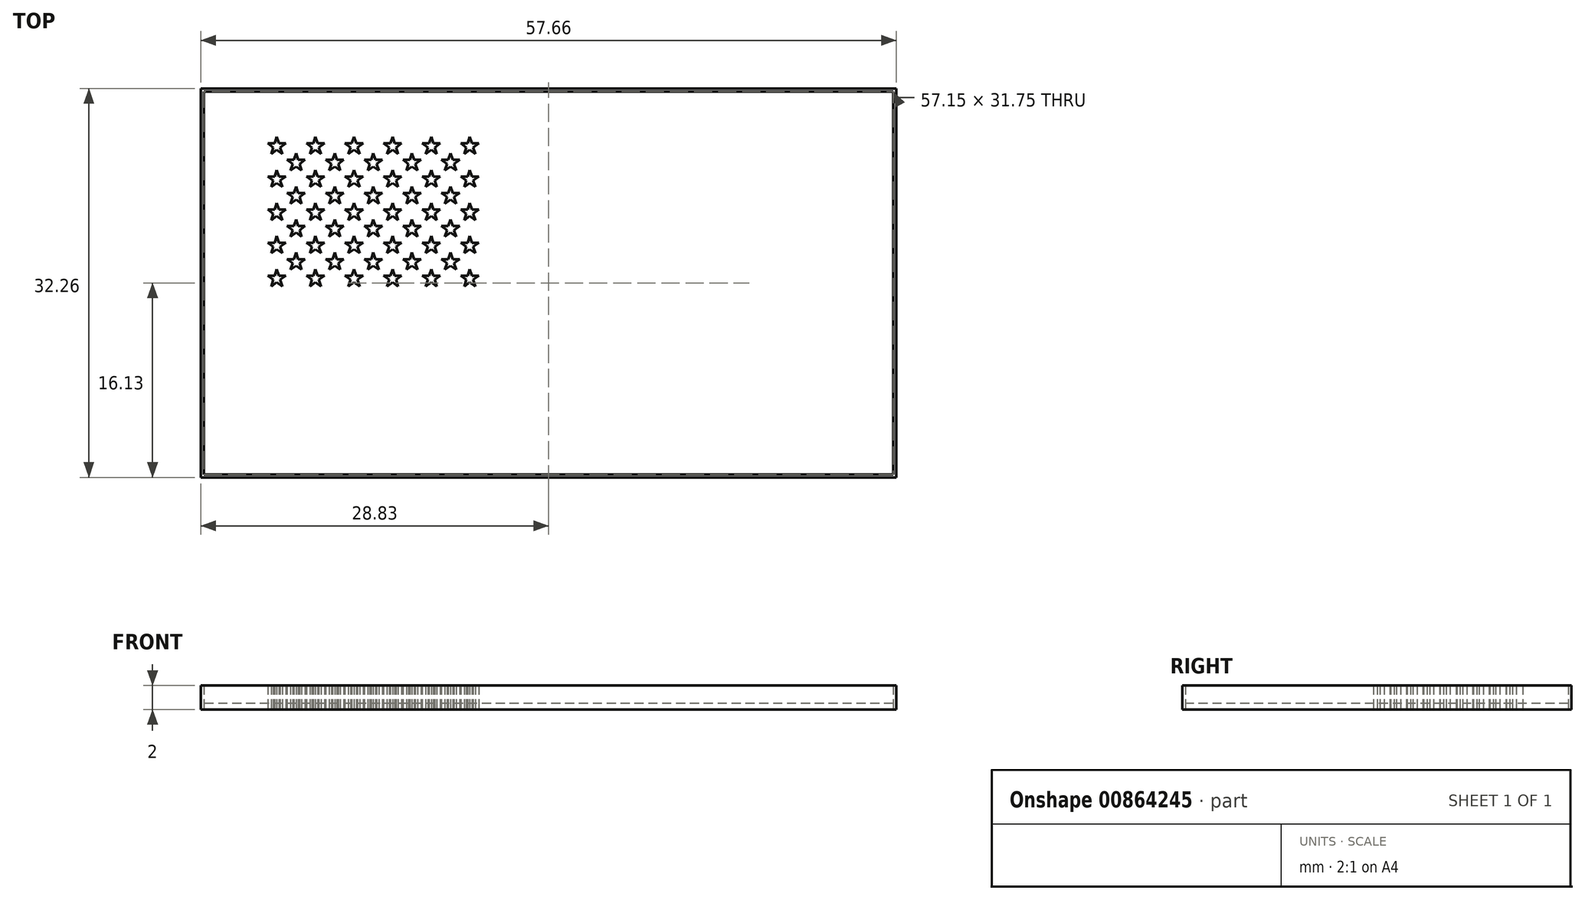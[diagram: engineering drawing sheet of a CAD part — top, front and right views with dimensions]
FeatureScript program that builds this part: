
annotation { "Feature Type Name" : "Feature", "Feature Type Description" : "" }
export const myFeature = defineFeature(function(context is Context, id is Id, definition is map)
    precondition{}
    {
        {
            var Q0;
            Q0=qCreatedBy(makeId("Top.planeOp"),FACE);
            var sketch = newSketch(context, id + "F0", { "sketchPlane" : qUnion([Q0])});
            skLineSegment(sketch, "E0.rect.bottom", {"start": v(24.13, 12.7) * mm, "end": v(-24.13, 12.7) * mm});
            skLineSegment(sketch, "E0.rect.top", {"start": v(24.13, -12.7) * mm, "end": v(-24.13, -12.7) * mm});
            skLineSegment(sketch, "E0.rect.left", {"start": v(24.13, 12.7) * mm, "end": v(24.13, -12.7) * mm});
            skLineSegment(sketch, "E0.rect.right", {"start": v(-24.13, 12.7) * mm, "end": v(-24.13, -12.7) * mm});
            skPoint(sketch, "E0.rect.middle", {"position": v(0, 0) * mm});
            skLineSegment(sketch, "E1.bottom", {"start": v(-24.13, 12.7) * mm, "end": v(-4.83, 12.7) * mm});
            skLineSegment(sketch, "E1.top", {"start": v(-24.13, -0.98) * mm, "end": v(-4.83, -0.98) * mm});
            skLineSegment(sketch, "E1.left", {"start": v(-24.13, 12.7) * mm, "end": v(-24.13, -0.98) * mm});
            skLineSegment(sketch, "E1.right", {"start": v(-4.83, 12.7) * mm, "end": v(-4.83, -0.98) * mm});
            skLineSegment(sketch, "E2.bottom", {"start": v(-4.83, 12.7) * mm, "end": v(24.13, 12.7) * mm});
            skLineSegment(sketch, "E2.top", {"start": v(-4.83, 10.75) * mm, "end": v(24.13, 10.75) * mm});
            skLineSegment(sketch, "E2.left", {"start": v(-4.83, 12.7) * mm, "end": v(-4.83, 10.75) * mm});
            skLineSegment(sketch, "E2.right", {"start": v(24.13, 12.7) * mm, "end": v(24.13, 10.75) * mm});
            skLineSegment(sketch, "E3.MirrorCS", {"start": v(-4.83, 8.8) * mm, "end": v(24.13, 8.8) * mm});
            skLineSegment(sketch, "E4.MirrorCS", {"start": v(-4.83, 6.84) * mm, "end": v(24.13, 6.84) * mm});
            skLineSegment(sketch, "E5.MirrorCS", {"start": v(-4.83, 4.89) * mm, "end": v(24.13, 4.89) * mm});
            skLineSegment(sketch, "E6.MirrorCS", {"start": v(-4.83, 2.93) * mm, "end": v(24.13, 2.93) * mm});
            skLineSegment(sketch, "E7.MirrorCS", {"start": v(-4.83, 0.98) * mm, "end": v(24.13, 0.98) * mm});
            skLineSegment(sketch, "E8.MirrorCS", {"start": v(-4.83, -0.97) * mm, "end": v(24.13, -0.97) * mm});
            skLineSegment(sketch, "E9.bottom", {"start": v(-24.13, -0.98) * mm, "end": v(24.13, -0.98) * mm});
            skLineSegment(sketch, "E9.top", {"start": v(-24.13, -2.93) * mm, "end": v(24.13, -2.93) * mm});
            skLineSegment(sketch, "E9.left", {"start": v(-24.13, -0.98) * mm, "end": v(-24.13, -2.93) * mm});
            skLineSegment(sketch, "E9.right", {"start": v(24.13, -0.98) * mm, "end": v(24.13, -2.93) * mm});
            skLineSegment(sketch, "E10.MirrorCS", {"start": v(-24.13, -4.88) * mm, "end": v(24.13, -4.88) * mm});
            skLineSegment(sketch, "E11.MirrorCS", {"start": v(-24.13, -6.84) * mm, "end": v(24.13, -6.84) * mm});
            skLineSegment(sketch, "E12.MirrorCS", {"start": v(-24.13, -8.8) * mm, "end": v(24.13, -8.8) * mm});
            skLineSegment(sketch, "E13.MirrorCS", {"start": v(-24.13, -10.74) * mm, "end": v(24.13, -10.74) * mm});
            skLineSegment(sketch, "E14.bottom", {"start": v(-24.13, 12.7) * mm, "end": v(-22.53, 12.7) * mm});
            skLineSegment(sketch, "E14.left", {"start": v(-24.13, 12.7) * mm, "end": v(-24.13, 11.33) * mm});
            skPoint(sketch, "E15.cCircle.perimeterSnap0", {"position": v(-22.53, 12.01) * mm});
            skPoint(sketch, "E15.0.startSnap0", {"position": v(-22.53, 12.01) * mm});
            skLineSegment(sketch, "E16", {"start": v(-22.53, 12.12) * mm, "end": v(-22.35, 11.57) * mm});
            skLineSegment(sketch, "E17", {"start": v(-21.78, 11.57) * mm, "end": v(-22.35, 11.57) * mm});
            skLineSegment(sketch, "E18", {"start": v(-23, 10.7) * mm, "end": v(-22.82, 11.24) * mm});
            skLineSegment(sketch, "E19", {"start": v(-23.28, 11.57) * mm, "end": v(-22.82, 11.24) * mm});
            skLineSegment(sketch, "E20", {"start": v(-21.78, 11.57) * mm, "end": v(-22.24, 11.24) * mm});
            skLineSegment(sketch, "E21.trimOffspring", {"start": v(-22.24, 11.24) * mm, "end": v(-22.07, 10.7) * mm});
            skLineSegment(sketch, "E22.trimOffspring", {"start": v(-22.53, 11.03) * mm, "end": v(-23, 10.7) * mm});
            skLineSegment(sketch, "E23.trimOffspring", {"start": v(-22.53, 11.03) * mm, "end": v(-22.07, 10.7) * mm});
            skLineSegment(sketch, "E24.trimOffspring", {"start": v(-22.7, 11.57) * mm, "end": v(-22.53, 12.12) * mm});
            skLineSegment(sketch, "E25.trimOffspring", {"start": v(-22.7, 11.57) * mm, "end": v(-23.28, 11.57) * mm});
            skLineSegment(sketch, "E26.0.1.0", {"start": v(-22.53, 9.37) * mm, "end": v(-22.35, 8.83) * mm});
            skLineSegment(sketch, "E26.0.1.1", {"start": v(-21.78, 8.83) * mm, "end": v(-22.35, 8.83) * mm});
            skLineSegment(sketch, "E26.0.1.2", {"start": v(-21.78, 8.83) * mm, "end": v(-22.24, 8.5) * mm});
            skLineSegment(sketch, "E26.0.1.3", {"start": v(-22.24, 8.5) * mm, "end": v(-22.07, 7.95) * mm});
            skLineSegment(sketch, "E26.0.1.4", {"start": v(-22.53, 8.28) * mm, "end": v(-22.07, 7.95) * mm});
            skLineSegment(sketch, "E26.0.1.5", {"start": v(-22.53, 8.28) * mm, "end": v(-23, 7.95) * mm});
            skLineSegment(sketch, "E26.0.1.6", {"start": v(-23, 7.95) * mm, "end": v(-22.82, 8.5) * mm});
            skLineSegment(sketch, "E26.0.1.7", {"start": v(-23.28, 8.83) * mm, "end": v(-22.82, 8.5) * mm});
            skLineSegment(sketch, "E26.0.1.8", {"start": v(-22.7, 8.83) * mm, "end": v(-22.53, 9.37) * mm});
            skLineSegment(sketch, "E26.0.1.9", {"start": v(-22.7, 8.83) * mm, "end": v(-23.28, 8.83) * mm});
            skLineSegment(sketch, "E26.0.2.0", {"start": v(-22.53, 6.63) * mm, "end": v(-22.35, 6.09) * mm});
            skLineSegment(sketch, "E26.0.2.1", {"start": v(-21.78, 6.09) * mm, "end": v(-22.35, 6.09) * mm});
            skLineSegment(sketch, "E26.0.2.2", {"start": v(-21.78, 6.09) * mm, "end": v(-22.24, 5.75) * mm});
            skLineSegment(sketch, "E26.0.2.3", {"start": v(-22.24, 5.75) * mm, "end": v(-22.07, 5.2) * mm});
            skLineSegment(sketch, "E26.0.2.4", {"start": v(-22.53, 5.54) * mm, "end": v(-22.07, 5.2) * mm});
            skLineSegment(sketch, "E26.0.2.5", {"start": v(-22.53, 5.54) * mm, "end": v(-23, 5.2) * mm});
            skLineSegment(sketch, "E26.0.2.6", {"start": v(-23, 5.2) * mm, "end": v(-22.82, 5.75) * mm});
            skLineSegment(sketch, "E26.0.2.7", {"start": v(-23.28, 6.09) * mm, "end": v(-22.82, 5.75) * mm});
            skLineSegment(sketch, "E26.0.2.8", {"start": v(-22.7, 6.09) * mm, "end": v(-22.53, 6.63) * mm});
            skLineSegment(sketch, "E26.0.2.9", {"start": v(-22.7, 6.09) * mm, "end": v(-23.28, 6.09) * mm});
            skLineSegment(sketch, "E26.0.3.0", {"start": v(-22.53, 3.89) * mm, "end": v(-22.35, 3.34) * mm});
            skLineSegment(sketch, "E26.0.3.1", {"start": v(-21.78, 3.34) * mm, "end": v(-22.35, 3.34) * mm});
            skLineSegment(sketch, "E26.0.3.2", {"start": v(-21.78, 3.34) * mm, "end": v(-22.24, 3) * mm});
            skLineSegment(sketch, "E26.0.3.3", {"start": v(-22.24, 3) * mm, "end": v(-22.07, 2.46) * mm});
            skLineSegment(sketch, "E26.0.3.4", {"start": v(-22.53, 2.8) * mm, "end": v(-22.07, 2.46) * mm});
            skLineSegment(sketch, "E26.0.3.5", {"start": v(-22.53, 2.8) * mm, "end": v(-23, 2.46) * mm});
            skLineSegment(sketch, "E26.0.3.6", {"start": v(-23, 2.46) * mm, "end": v(-22.82, 3) * mm});
            skLineSegment(sketch, "E26.0.3.7", {"start": v(-23.28, 3.34) * mm, "end": v(-22.82, 3) * mm});
            skLineSegment(sketch, "E26.0.3.8", {"start": v(-22.7, 3.34) * mm, "end": v(-22.53, 3.89) * mm});
            skLineSegment(sketch, "E26.0.3.9", {"start": v(-22.7, 3.34) * mm, "end": v(-23.28, 3.34) * mm});
            skLineSegment(sketch, "E26.0.4.0", {"start": v(-22.53, 1.14) * mm, "end": v(-22.35, 0.6) * mm});
            skLineSegment(sketch, "E26.0.4.1", {"start": v(-21.78, 0.6) * mm, "end": v(-22.35, 0.6) * mm});
            skLineSegment(sketch, "E26.0.4.2", {"start": v(-21.78, 0.6) * mm, "end": v(-22.24, 0.26) * mm});
            skLineSegment(sketch, "E26.0.4.3", {"start": v(-22.24, 0.26) * mm, "end": v(-22.07, -0.28) * mm});
            skLineSegment(sketch, "E26.0.4.4", {"start": v(-22.53, 0.05) * mm, "end": v(-22.07, -0.28) * mm});
            skLineSegment(sketch, "E26.0.4.5", {"start": v(-22.53, 0.05) * mm, "end": v(-23, -0.28) * mm});
            skLineSegment(sketch, "E26.0.4.6", {"start": v(-23, -0.28) * mm, "end": v(-22.82, 0.26) * mm});
            skLineSegment(sketch, "E26.0.4.7", {"start": v(-23.28, 0.6) * mm, "end": v(-22.82, 0.26) * mm});
            skLineSegment(sketch, "E26.0.4.8", {"start": v(-22.7, 0.6) * mm, "end": v(-22.53, 1.14) * mm});
            skLineSegment(sketch, "E26.0.4.9", {"start": v(-22.7, 0.6) * mm, "end": v(-23.28, 0.6) * mm});
            skLineSegment(sketch, "E26.1.0.0", {"start": v(-19.33, 12.12) * mm, "end": v(-19.15, 11.57) * mm});
            skLineSegment(sketch, "E26.1.0.1", {"start": v(-18.58, 11.57) * mm, "end": v(-19.15, 11.57) * mm});
            skLineSegment(sketch, "E26.1.0.2", {"start": v(-18.58, 11.57) * mm, "end": v(-19.04, 11.24) * mm});
            skLineSegment(sketch, "E26.1.0.3", {"start": v(-19.04, 11.24) * mm, "end": v(-18.87, 10.7) * mm});
            skLineSegment(sketch, "E26.1.0.4", {"start": v(-19.33, 11.03) * mm, "end": v(-18.87, 10.7) * mm});
            skLineSegment(sketch, "E26.1.0.5", {"start": v(-19.33, 11.03) * mm, "end": v(-19.8, 10.7) * mm});
            skLineSegment(sketch, "E26.1.0.6", {"start": v(-19.8, 10.7) * mm, "end": v(-19.62, 11.24) * mm});
            skLineSegment(sketch, "E26.1.0.7", {"start": v(-20.08, 11.57) * mm, "end": v(-19.62, 11.24) * mm});
            skLineSegment(sketch, "E26.1.0.8", {"start": v(-19.5, 11.57) * mm, "end": v(-19.33, 12.12) * mm});
            skLineSegment(sketch, "E26.1.0.9", {"start": v(-19.5, 11.57) * mm, "end": v(-20.08, 11.57) * mm});
            skLineSegment(sketch, "E26.1.1.0", {"start": v(-19.33, 9.37) * mm, "end": v(-19.15, 8.83) * mm});
            skLineSegment(sketch, "E26.1.1.1", {"start": v(-18.58, 8.83) * mm, "end": v(-19.15, 8.83) * mm});
            skLineSegment(sketch, "E26.1.1.2", {"start": v(-18.58, 8.83) * mm, "end": v(-19.04, 8.5) * mm});
            skLineSegment(sketch, "E26.1.1.3", {"start": v(-19.04, 8.5) * mm, "end": v(-18.87, 7.95) * mm});
            skLineSegment(sketch, "E26.1.1.4", {"start": v(-19.33, 8.28) * mm, "end": v(-18.87, 7.95) * mm});
            skLineSegment(sketch, "E26.1.1.5", {"start": v(-19.33, 8.28) * mm, "end": v(-19.8, 7.95) * mm});
            skLineSegment(sketch, "E26.1.1.6", {"start": v(-19.8, 7.95) * mm, "end": v(-19.62, 8.5) * mm});
            skLineSegment(sketch, "E26.1.1.7", {"start": v(-20.08, 8.83) * mm, "end": v(-19.62, 8.5) * mm});
            skLineSegment(sketch, "E26.1.1.8", {"start": v(-19.5, 8.83) * mm, "end": v(-19.33, 9.37) * mm});
            skLineSegment(sketch, "E26.1.1.9", {"start": v(-19.5, 8.83) * mm, "end": v(-20.08, 8.83) * mm});
            skLineSegment(sketch, "E26.1.2.0", {"start": v(-19.33, 6.63) * mm, "end": v(-19.15, 6.09) * mm});
            skLineSegment(sketch, "E26.1.2.1", {"start": v(-18.58, 6.09) * mm, "end": v(-19.15, 6.09) * mm});
            skLineSegment(sketch, "E26.1.2.2", {"start": v(-18.58, 6.09) * mm, "end": v(-19.04, 5.75) * mm});
            skLineSegment(sketch, "E26.1.2.3", {"start": v(-19.04, 5.75) * mm, "end": v(-18.87, 5.2) * mm});
            skLineSegment(sketch, "E26.1.2.4", {"start": v(-19.33, 5.54) * mm, "end": v(-18.87, 5.2) * mm});
            skLineSegment(sketch, "E26.1.2.5", {"start": v(-19.33, 5.54) * mm, "end": v(-19.8, 5.2) * mm});
            skLineSegment(sketch, "E26.1.2.6", {"start": v(-19.8, 5.2) * mm, "end": v(-19.62, 5.75) * mm});
            skLineSegment(sketch, "E26.1.2.7", {"start": v(-20.08, 6.09) * mm, "end": v(-19.62, 5.75) * mm});
            skLineSegment(sketch, "E26.1.2.8", {"start": v(-19.5, 6.09) * mm, "end": v(-19.33, 6.63) * mm});
            skLineSegment(sketch, "E26.1.2.9", {"start": v(-19.5, 6.09) * mm, "end": v(-20.08, 6.09) * mm});
            skLineSegment(sketch, "E26.1.3.0", {"start": v(-19.33, 3.89) * mm, "end": v(-19.15, 3.34) * mm});
            skLineSegment(sketch, "E26.1.3.1", {"start": v(-18.58, 3.34) * mm, "end": v(-19.15, 3.34) * mm});
            skLineSegment(sketch, "E26.1.3.2", {"start": v(-18.58, 3.34) * mm, "end": v(-19.04, 3) * mm});
            skLineSegment(sketch, "E26.1.3.3", {"start": v(-19.04, 3) * mm, "end": v(-18.87, 2.46) * mm});
            skLineSegment(sketch, "E26.1.3.4", {"start": v(-19.33, 2.8) * mm, "end": v(-18.87, 2.46) * mm});
            skLineSegment(sketch, "E26.1.3.5", {"start": v(-19.33, 2.8) * mm, "end": v(-19.8, 2.46) * mm});
            skLineSegment(sketch, "E26.1.3.6", {"start": v(-19.8, 2.46) * mm, "end": v(-19.62, 3) * mm});
            skLineSegment(sketch, "E26.1.3.7", {"start": v(-20.08, 3.34) * mm, "end": v(-19.62, 3) * mm});
            skLineSegment(sketch, "E26.1.3.8", {"start": v(-19.5, 3.34) * mm, "end": v(-19.33, 3.89) * mm});
            skLineSegment(sketch, "E26.1.3.9", {"start": v(-19.5, 3.34) * mm, "end": v(-20.08, 3.34) * mm});
            skLineSegment(sketch, "E26.1.4.0", {"start": v(-19.33, 1.14) * mm, "end": v(-19.15, 0.6) * mm});
            skLineSegment(sketch, "E26.1.4.1", {"start": v(-18.58, 0.6) * mm, "end": v(-19.15, 0.6) * mm});
            skLineSegment(sketch, "E26.1.4.2", {"start": v(-18.58, 0.6) * mm, "end": v(-19.04, 0.26) * mm});
            skLineSegment(sketch, "E26.1.4.3", {"start": v(-19.04, 0.26) * mm, "end": v(-18.87, -0.28) * mm});
            skLineSegment(sketch, "E26.1.4.4", {"start": v(-19.33, 0.05) * mm, "end": v(-18.87, -0.28) * mm});
            skLineSegment(sketch, "E26.1.4.5", {"start": v(-19.33, 0.05) * mm, "end": v(-19.8, -0.28) * mm});
            skLineSegment(sketch, "E26.1.4.6", {"start": v(-19.8, -0.28) * mm, "end": v(-19.62, 0.26) * mm});
            skLineSegment(sketch, "E26.1.4.7", {"start": v(-20.08, 0.6) * mm, "end": v(-19.62, 0.26) * mm});
            skLineSegment(sketch, "E26.1.4.8", {"start": v(-19.5, 0.6) * mm, "end": v(-19.33, 1.14) * mm});
            skLineSegment(sketch, "E26.1.4.9", {"start": v(-19.5, 0.6) * mm, "end": v(-20.08, 0.6) * mm});
            skLineSegment(sketch, "E26.2.0.0", {"start": v(-16.13, 12.12) * mm, "end": v(-15.95, 11.57) * mm});
            skLineSegment(sketch, "E26.2.0.1", {"start": v(-15.38, 11.57) * mm, "end": v(-15.95, 11.57) * mm});
            skLineSegment(sketch, "E26.2.0.2", {"start": v(-15.38, 11.57) * mm, "end": v(-15.84, 11.24) * mm});
            skLineSegment(sketch, "E26.2.0.3", {"start": v(-15.84, 11.24) * mm, "end": v(-15.67, 10.7) * mm});
            skLineSegment(sketch, "E26.2.0.4", {"start": v(-16.13, 11.03) * mm, "end": v(-15.67, 10.7) * mm});
            skLineSegment(sketch, "E26.2.0.5", {"start": v(-16.13, 11.03) * mm, "end": v(-16.6, 10.7) * mm});
            skLineSegment(sketch, "E26.2.0.6", {"start": v(-16.6, 10.7) * mm, "end": v(-16.42, 11.24) * mm});
            skLineSegment(sketch, "E26.2.0.7", {"start": v(-16.88, 11.57) * mm, "end": v(-16.42, 11.24) * mm});
            skLineSegment(sketch, "E26.2.0.8", {"start": v(-16.3, 11.57) * mm, "end": v(-16.13, 12.12) * mm});
            skLineSegment(sketch, "E26.2.0.9", {"start": v(-16.3, 11.57) * mm, "end": v(-16.88, 11.57) * mm});
            skLineSegment(sketch, "E26.2.1.0", {"start": v(-16.13, 9.37) * mm, "end": v(-15.95, 8.83) * mm});
            skLineSegment(sketch, "E26.2.1.1", {"start": v(-15.38, 8.83) * mm, "end": v(-15.95, 8.83) * mm});
            skLineSegment(sketch, "E26.2.1.2", {"start": v(-15.38, 8.83) * mm, "end": v(-15.84, 8.5) * mm});
            skLineSegment(sketch, "E26.2.1.3", {"start": v(-15.84, 8.5) * mm, "end": v(-15.67, 7.95) * mm});
            skLineSegment(sketch, "E26.2.1.4", {"start": v(-16.13, 8.28) * mm, "end": v(-15.67, 7.95) * mm});
            skLineSegment(sketch, "E26.2.1.5", {"start": v(-16.13, 8.28) * mm, "end": v(-16.6, 7.95) * mm});
            skLineSegment(sketch, "E26.2.1.6", {"start": v(-16.6, 7.95) * mm, "end": v(-16.42, 8.5) * mm});
            skLineSegment(sketch, "E26.2.1.7", {"start": v(-16.88, 8.83) * mm, "end": v(-16.42, 8.5) * mm});
            skLineSegment(sketch, "E26.2.1.8", {"start": v(-16.3, 8.83) * mm, "end": v(-16.13, 9.37) * mm});
            skLineSegment(sketch, "E26.2.1.9", {"start": v(-16.3, 8.83) * mm, "end": v(-16.88, 8.83) * mm});
            skLineSegment(sketch, "E26.2.2.0", {"start": v(-16.13, 6.63) * mm, "end": v(-15.95, 6.09) * mm});
            skLineSegment(sketch, "E26.2.2.1", {"start": v(-15.38, 6.09) * mm, "end": v(-15.95, 6.09) * mm});
            skLineSegment(sketch, "E26.2.2.2", {"start": v(-15.38, 6.09) * mm, "end": v(-15.84, 5.75) * mm});
            skLineSegment(sketch, "E26.2.2.3", {"start": v(-15.84, 5.75) * mm, "end": v(-15.67, 5.2) * mm});
            skLineSegment(sketch, "E26.2.2.4", {"start": v(-16.13, 5.54) * mm, "end": v(-15.67, 5.2) * mm});
            skLineSegment(sketch, "E26.2.2.5", {"start": v(-16.13, 5.54) * mm, "end": v(-16.6, 5.2) * mm});
            skLineSegment(sketch, "E26.2.2.6", {"start": v(-16.6, 5.2) * mm, "end": v(-16.42, 5.75) * mm});
            skLineSegment(sketch, "E26.2.2.7", {"start": v(-16.88, 6.09) * mm, "end": v(-16.42, 5.75) * mm});
            skLineSegment(sketch, "E26.2.2.8", {"start": v(-16.3, 6.09) * mm, "end": v(-16.13, 6.63) * mm});
            skLineSegment(sketch, "E26.2.2.9", {"start": v(-16.3, 6.09) * mm, "end": v(-16.88, 6.09) * mm});
            skLineSegment(sketch, "E26.2.3.0", {"start": v(-16.13, 3.89) * mm, "end": v(-15.95, 3.34) * mm});
            skLineSegment(sketch, "E26.2.3.1", {"start": v(-15.38, 3.34) * mm, "end": v(-15.95, 3.34) * mm});
            skLineSegment(sketch, "E26.2.3.2", {"start": v(-15.38, 3.34) * mm, "end": v(-15.84, 3) * mm});
            skLineSegment(sketch, "E26.2.3.3", {"start": v(-15.84, 3) * mm, "end": v(-15.67, 2.46) * mm});
            skLineSegment(sketch, "E26.2.3.4", {"start": v(-16.13, 2.8) * mm, "end": v(-15.67, 2.46) * mm});
            skLineSegment(sketch, "E26.2.3.5", {"start": v(-16.13, 2.8) * mm, "end": v(-16.6, 2.46) * mm});
            skLineSegment(sketch, "E26.2.3.6", {"start": v(-16.6, 2.46) * mm, "end": v(-16.42, 3) * mm});
            skLineSegment(sketch, "E26.2.3.7", {"start": v(-16.88, 3.34) * mm, "end": v(-16.42, 3) * mm});
            skLineSegment(sketch, "E26.2.3.8", {"start": v(-16.3, 3.34) * mm, "end": v(-16.13, 3.89) * mm});
            skLineSegment(sketch, "E26.2.3.9", {"start": v(-16.3, 3.34) * mm, "end": v(-16.88, 3.34) * mm});
            skLineSegment(sketch, "E26.2.4.0", {"start": v(-16.13, 1.14) * mm, "end": v(-15.95, 0.6) * mm});
            skLineSegment(sketch, "E26.2.4.1", {"start": v(-15.38, 0.6) * mm, "end": v(-15.95, 0.6) * mm});
            skLineSegment(sketch, "E26.2.4.2", {"start": v(-15.38, 0.6) * mm, "end": v(-15.84, 0.26) * mm});
            skLineSegment(sketch, "E26.2.4.3", {"start": v(-15.84, 0.26) * mm, "end": v(-15.67, -0.28) * mm});
            skLineSegment(sketch, "E26.2.4.4", {"start": v(-16.13, 0.05) * mm, "end": v(-15.67, -0.28) * mm});
            skLineSegment(sketch, "E26.2.4.5", {"start": v(-16.13, 0.05) * mm, "end": v(-16.6, -0.28) * mm});
            skLineSegment(sketch, "E26.2.4.6", {"start": v(-16.6, -0.28) * mm, "end": v(-16.42, 0.26) * mm});
            skLineSegment(sketch, "E26.2.4.7", {"start": v(-16.88, 0.6) * mm, "end": v(-16.42, 0.26) * mm});
            skLineSegment(sketch, "E26.2.4.8", {"start": v(-16.3, 0.6) * mm, "end": v(-16.13, 1.14) * mm});
            skLineSegment(sketch, "E26.2.4.9", {"start": v(-16.3, 0.6) * mm, "end": v(-16.88, 0.6) * mm});
            skLineSegment(sketch, "E26.3.0.0", {"start": v(-12.93, 12.12) * mm, "end": v(-12.75, 11.57) * mm});
            skLineSegment(sketch, "E26.3.0.1", {"start": v(-12.18, 11.57) * mm, "end": v(-12.75, 11.57) * mm});
            skLineSegment(sketch, "E26.3.0.2", {"start": v(-12.18, 11.57) * mm, "end": v(-12.64, 11.24) * mm});
            skLineSegment(sketch, "E26.3.0.3", {"start": v(-12.64, 11.24) * mm, "end": v(-12.47, 10.7) * mm});
            skLineSegment(sketch, "E26.3.0.4", {"start": v(-12.93, 11.03) * mm, "end": v(-12.47, 10.7) * mm});
            skLineSegment(sketch, "E26.3.0.5", {"start": v(-12.93, 11.03) * mm, "end": v(-13.4, 10.7) * mm});
            skLineSegment(sketch, "E26.3.0.6", {"start": v(-13.4, 10.7) * mm, "end": v(-13.21, 11.24) * mm});
            skLineSegment(sketch, "E26.3.0.7", {"start": v(-13.68, 11.57) * mm, "end": v(-13.21, 11.24) * mm});
            skLineSegment(sketch, "E26.3.0.8", {"start": v(-13.1, 11.57) * mm, "end": v(-12.93, 12.12) * mm});
            skLineSegment(sketch, "E26.3.0.9", {"start": v(-13.1, 11.57) * mm, "end": v(-13.68, 11.57) * mm});
            skLineSegment(sketch, "E26.3.1.0", {"start": v(-12.93, 9.37) * mm, "end": v(-12.75, 8.83) * mm});
            skLineSegment(sketch, "E26.3.1.1", {"start": v(-12.18, 8.83) * mm, "end": v(-12.75, 8.83) * mm});
            skLineSegment(sketch, "E26.3.1.2", {"start": v(-12.18, 8.83) * mm, "end": v(-12.64, 8.5) * mm});
            skLineSegment(sketch, "E26.3.1.3", {"start": v(-12.64, 8.5) * mm, "end": v(-12.47, 7.95) * mm});
            skLineSegment(sketch, "E26.3.1.4", {"start": v(-12.93, 8.28) * mm, "end": v(-12.47, 7.95) * mm});
            skLineSegment(sketch, "E26.3.1.5", {"start": v(-12.93, 8.28) * mm, "end": v(-13.4, 7.95) * mm});
            skLineSegment(sketch, "E26.3.1.6", {"start": v(-13.4, 7.95) * mm, "end": v(-13.21, 8.5) * mm});
            skLineSegment(sketch, "E26.3.1.7", {"start": v(-13.68, 8.83) * mm, "end": v(-13.21, 8.5) * mm});
            skLineSegment(sketch, "E26.3.1.8", {"start": v(-13.1, 8.83) * mm, "end": v(-12.93, 9.37) * mm});
            skLineSegment(sketch, "E26.3.1.9", {"start": v(-13.1, 8.83) * mm, "end": v(-13.68, 8.83) * mm});
            skLineSegment(sketch, "E26.3.2.0", {"start": v(-12.93, 6.63) * mm, "end": v(-12.75, 6.09) * mm});
            skLineSegment(sketch, "E26.3.2.1", {"start": v(-12.18, 6.09) * mm, "end": v(-12.75, 6.09) * mm});
            skLineSegment(sketch, "E26.3.2.2", {"start": v(-12.18, 6.09) * mm, "end": v(-12.64, 5.75) * mm});
            skLineSegment(sketch, "E26.3.2.3", {"start": v(-12.64, 5.75) * mm, "end": v(-12.47, 5.2) * mm});
            skLineSegment(sketch, "E26.3.2.4", {"start": v(-12.93, 5.54) * mm, "end": v(-12.47, 5.2) * mm});
            skLineSegment(sketch, "E26.3.2.5", {"start": v(-12.93, 5.54) * mm, "end": v(-13.4, 5.2) * mm});
            skLineSegment(sketch, "E26.3.2.6", {"start": v(-13.4, 5.2) * mm, "end": v(-13.21, 5.75) * mm});
            skLineSegment(sketch, "E26.3.2.7", {"start": v(-13.68, 6.09) * mm, "end": v(-13.21, 5.75) * mm});
            skLineSegment(sketch, "E26.3.2.8", {"start": v(-13.1, 6.09) * mm, "end": v(-12.93, 6.63) * mm});
            skLineSegment(sketch, "E26.3.2.9", {"start": v(-13.1, 6.09) * mm, "end": v(-13.68, 6.09) * mm});
            skLineSegment(sketch, "E26.3.3.0", {"start": v(-12.93, 3.89) * mm, "end": v(-12.75, 3.34) * mm});
            skLineSegment(sketch, "E26.3.3.1", {"start": v(-12.18, 3.34) * mm, "end": v(-12.75, 3.34) * mm});
            skLineSegment(sketch, "E26.3.3.2", {"start": v(-12.18, 3.34) * mm, "end": v(-12.64, 3) * mm});
            skLineSegment(sketch, "E26.3.3.3", {"start": v(-12.64, 3) * mm, "end": v(-12.47, 2.46) * mm});
            skLineSegment(sketch, "E26.3.3.4", {"start": v(-12.93, 2.8) * mm, "end": v(-12.47, 2.46) * mm});
            skLineSegment(sketch, "E26.3.3.5", {"start": v(-12.93, 2.8) * mm, "end": v(-13.4, 2.46) * mm});
            skLineSegment(sketch, "E26.3.3.6", {"start": v(-13.4, 2.46) * mm, "end": v(-13.21, 3) * mm});
            skLineSegment(sketch, "E26.3.3.7", {"start": v(-13.68, 3.34) * mm, "end": v(-13.21, 3) * mm});
            skLineSegment(sketch, "E26.3.3.8", {"start": v(-13.1, 3.34) * mm, "end": v(-12.93, 3.89) * mm});
            skLineSegment(sketch, "E26.3.3.9", {"start": v(-13.1, 3.34) * mm, "end": v(-13.68, 3.34) * mm});
            skLineSegment(sketch, "E26.3.4.0", {"start": v(-12.93, 1.14) * mm, "end": v(-12.75, 0.6) * mm});
            skLineSegment(sketch, "E26.3.4.1", {"start": v(-12.18, 0.6) * mm, "end": v(-12.75, 0.6) * mm});
            skLineSegment(sketch, "E26.3.4.2", {"start": v(-12.18, 0.6) * mm, "end": v(-12.64, 0.26) * mm});
            skLineSegment(sketch, "E26.3.4.3", {"start": v(-12.64, 0.26) * mm, "end": v(-12.47, -0.28) * mm});
            skLineSegment(sketch, "E26.3.4.4", {"start": v(-12.93, 0.05) * mm, "end": v(-12.47, -0.28) * mm});
            skLineSegment(sketch, "E26.3.4.5", {"start": v(-12.93, 0.05) * mm, "end": v(-13.4, -0.28) * mm});
            skLineSegment(sketch, "E26.3.4.6", {"start": v(-13.4, -0.28) * mm, "end": v(-13.21, 0.26) * mm});
            skLineSegment(sketch, "E26.3.4.7", {"start": v(-13.68, 0.6) * mm, "end": v(-13.21, 0.26) * mm});
            skLineSegment(sketch, "E26.3.4.8", {"start": v(-13.1, 0.6) * mm, "end": v(-12.93, 1.14) * mm});
            skLineSegment(sketch, "E26.3.4.9", {"start": v(-13.1, 0.6) * mm, "end": v(-13.68, 0.6) * mm});
            skLineSegment(sketch, "E26.4.0.0", {"start": v(-9.73, 12.12) * mm, "end": v(-9.55, 11.57) * mm});
            skLineSegment(sketch, "E26.4.0.1", {"start": v(-8.98, 11.57) * mm, "end": v(-9.55, 11.57) * mm});
            skLineSegment(sketch, "E26.4.0.2", {"start": v(-8.98, 11.57) * mm, "end": v(-9.44, 11.24) * mm});
            skLineSegment(sketch, "E26.4.0.3", {"start": v(-9.44, 11.24) * mm, "end": v(-9.27, 10.7) * mm});
            skLineSegment(sketch, "E26.4.0.4", {"start": v(-9.73, 11.03) * mm, "end": v(-9.27, 10.7) * mm});
            skLineSegment(sketch, "E26.4.0.5", {"start": v(-9.73, 11.03) * mm, "end": v(-10.2, 10.7) * mm});
            skLineSegment(sketch, "E26.4.0.6", {"start": v(-10.2, 10.7) * mm, "end": v(-10.01, 11.24) * mm});
            skLineSegment(sketch, "E26.4.0.7", {"start": v(-10.48, 11.57) * mm, "end": v(-10.01, 11.24) * mm});
            skLineSegment(sketch, "E26.4.0.8", {"start": v(-9.9, 11.57) * mm, "end": v(-9.73, 12.12) * mm});
            skLineSegment(sketch, "E26.4.0.9", {"start": v(-9.9, 11.57) * mm, "end": v(-10.48, 11.57) * mm});
            skLineSegment(sketch, "E26.4.1.0", {"start": v(-9.73, 9.37) * mm, "end": v(-9.55, 8.83) * mm});
            skLineSegment(sketch, "E26.4.1.1", {"start": v(-8.98, 8.83) * mm, "end": v(-9.55, 8.83) * mm});
            skLineSegment(sketch, "E26.4.1.2", {"start": v(-8.98, 8.83) * mm, "end": v(-9.44, 8.5) * mm});
            skLineSegment(sketch, "E26.4.1.3", {"start": v(-9.44, 8.5) * mm, "end": v(-9.27, 7.95) * mm});
            skLineSegment(sketch, "E26.4.1.4", {"start": v(-9.73, 8.28) * mm, "end": v(-9.27, 7.95) * mm});
            skLineSegment(sketch, "E26.4.1.5", {"start": v(-9.73, 8.28) * mm, "end": v(-10.2, 7.95) * mm});
            skLineSegment(sketch, "E26.4.1.6", {"start": v(-10.2, 7.95) * mm, "end": v(-10.01, 8.5) * mm});
            skLineSegment(sketch, "E26.4.1.7", {"start": v(-10.48, 8.83) * mm, "end": v(-10.01, 8.5) * mm});
            skLineSegment(sketch, "E26.4.1.8", {"start": v(-9.9, 8.83) * mm, "end": v(-9.73, 9.37) * mm});
            skLineSegment(sketch, "E26.4.1.9", {"start": v(-9.9, 8.83) * mm, "end": v(-10.48, 8.83) * mm});
            skLineSegment(sketch, "E26.4.2.0", {"start": v(-9.73, 6.63) * mm, "end": v(-9.55, 6.09) * mm});
            skLineSegment(sketch, "E26.4.2.1", {"start": v(-8.98, 6.09) * mm, "end": v(-9.55, 6.09) * mm});
            skLineSegment(sketch, "E26.4.2.2", {"start": v(-8.98, 6.09) * mm, "end": v(-9.44, 5.75) * mm});
            skLineSegment(sketch, "E26.4.2.3", {"start": v(-9.44, 5.75) * mm, "end": v(-9.27, 5.2) * mm});
            skLineSegment(sketch, "E26.4.2.4", {"start": v(-9.73, 5.54) * mm, "end": v(-9.27, 5.2) * mm});
            skLineSegment(sketch, "E26.4.2.5", {"start": v(-9.73, 5.54) * mm, "end": v(-10.2, 5.2) * mm});
            skLineSegment(sketch, "E26.4.2.6", {"start": v(-10.2, 5.2) * mm, "end": v(-10.01, 5.75) * mm});
            skLineSegment(sketch, "E26.4.2.7", {"start": v(-10.48, 6.09) * mm, "end": v(-10.01, 5.75) * mm});
            skLineSegment(sketch, "E26.4.2.8", {"start": v(-9.9, 6.09) * mm, "end": v(-9.73, 6.63) * mm});
            skLineSegment(sketch, "E26.4.2.9", {"start": v(-9.9, 6.09) * mm, "end": v(-10.48, 6.09) * mm});
            skLineSegment(sketch, "E26.4.3.0", {"start": v(-9.73, 3.89) * mm, "end": v(-9.55, 3.34) * mm});
            skLineSegment(sketch, "E26.4.3.1", {"start": v(-8.98, 3.34) * mm, "end": v(-9.55, 3.34) * mm});
            skLineSegment(sketch, "E26.4.3.2", {"start": v(-8.98, 3.34) * mm, "end": v(-9.44, 3) * mm});
            skLineSegment(sketch, "E26.4.3.3", {"start": v(-9.44, 3) * mm, "end": v(-9.27, 2.46) * mm});
            skLineSegment(sketch, "E26.4.3.4", {"start": v(-9.73, 2.8) * mm, "end": v(-9.27, 2.46) * mm});
            skLineSegment(sketch, "E26.4.3.5", {"start": v(-9.73, 2.8) * mm, "end": v(-10.2, 2.46) * mm});
            skLineSegment(sketch, "E26.4.3.6", {"start": v(-10.2, 2.46) * mm, "end": v(-10.01, 3) * mm});
            skLineSegment(sketch, "E26.4.3.7", {"start": v(-10.48, 3.34) * mm, "end": v(-10.01, 3) * mm});
            skLineSegment(sketch, "E26.4.3.8", {"start": v(-9.9, 3.34) * mm, "end": v(-9.73, 3.89) * mm});
            skLineSegment(sketch, "E26.4.3.9", {"start": v(-9.9, 3.34) * mm, "end": v(-10.48, 3.34) * mm});
            skLineSegment(sketch, "E26.4.4.0", {"start": v(-9.73, 1.14) * mm, "end": v(-9.55, 0.6) * mm});
            skLineSegment(sketch, "E26.4.4.1", {"start": v(-8.98, 0.6) * mm, "end": v(-9.55, 0.6) * mm});
            skLineSegment(sketch, "E26.4.4.2", {"start": v(-8.98, 0.6) * mm, "end": v(-9.44, 0.26) * mm});
            skLineSegment(sketch, "E26.4.4.3", {"start": v(-9.44, 0.26) * mm, "end": v(-9.27, -0.28) * mm});
            skLineSegment(sketch, "E26.4.4.4", {"start": v(-9.73, 0.05) * mm, "end": v(-9.27, -0.28) * mm});
            skLineSegment(sketch, "E26.4.4.5", {"start": v(-9.73, 0.05) * mm, "end": v(-10.2, -0.28) * mm});
            skLineSegment(sketch, "E26.4.4.6", {"start": v(-10.2, -0.28) * mm, "end": v(-10.01, 0.26) * mm});
            skLineSegment(sketch, "E26.4.4.7", {"start": v(-10.48, 0.6) * mm, "end": v(-10.01, 0.26) * mm});
            skLineSegment(sketch, "E26.4.4.8", {"start": v(-9.9, 0.6) * mm, "end": v(-9.73, 1.14) * mm});
            skLineSegment(sketch, "E26.4.4.9", {"start": v(-9.9, 0.6) * mm, "end": v(-10.48, 0.6) * mm});
            skLineSegment(sketch, "E26.5.0.0", {"start": v(-6.53, 12.12) * mm, "end": v(-6.35, 11.57) * mm});
            skLineSegment(sketch, "E26.5.0.1", {"start": v(-5.78, 11.57) * mm, "end": v(-6.35, 11.57) * mm});
            skLineSegment(sketch, "E26.5.0.2", {"start": v(-5.78, 11.57) * mm, "end": v(-6.24, 11.24) * mm});
            skLineSegment(sketch, "E26.5.0.3", {"start": v(-6.24, 11.24) * mm, "end": v(-6.06, 10.7) * mm});
            skLineSegment(sketch, "E26.5.0.4", {"start": v(-6.53, 11.03) * mm, "end": v(-6.06, 10.7) * mm});
            skLineSegment(sketch, "E26.5.0.5", {"start": v(-6.53, 11.03) * mm, "end": v(-7, 10.7) * mm});
            skLineSegment(sketch, "E26.5.0.6", {"start": v(-7, 10.7) * mm, "end": v(-6.81, 11.24) * mm});
            skLineSegment(sketch, "E26.5.0.7", {"start": v(-7.28, 11.57) * mm, "end": v(-6.81, 11.24) * mm});
            skLineSegment(sketch, "E26.5.0.8", {"start": v(-6.7, 11.57) * mm, "end": v(-6.53, 12.12) * mm});
            skLineSegment(sketch, "E26.5.0.9", {"start": v(-6.7, 11.57) * mm, "end": v(-7.28, 11.57) * mm});
            skLineSegment(sketch, "E26.5.1.0", {"start": v(-6.53, 9.37) * mm, "end": v(-6.35, 8.83) * mm});
            skLineSegment(sketch, "E26.5.1.1", {"start": v(-5.78, 8.83) * mm, "end": v(-6.35, 8.83) * mm});
            skLineSegment(sketch, "E26.5.1.2", {"start": v(-5.78, 8.83) * mm, "end": v(-6.24, 8.5) * mm});
            skLineSegment(sketch, "E26.5.1.3", {"start": v(-6.24, 8.5) * mm, "end": v(-6.06, 7.95) * mm});
            skLineSegment(sketch, "E26.5.1.4", {"start": v(-6.53, 8.28) * mm, "end": v(-6.06, 7.95) * mm});
            skLineSegment(sketch, "E26.5.1.5", {"start": v(-6.53, 8.28) * mm, "end": v(-7, 7.95) * mm});
            skLineSegment(sketch, "E26.5.1.6", {"start": v(-7, 7.95) * mm, "end": v(-6.81, 8.5) * mm});
            skLineSegment(sketch, "E26.5.1.7", {"start": v(-7.28, 8.83) * mm, "end": v(-6.81, 8.5) * mm});
            skLineSegment(sketch, "E26.5.1.8", {"start": v(-6.7, 8.83) * mm, "end": v(-6.53, 9.37) * mm});
            skLineSegment(sketch, "E26.5.1.9", {"start": v(-6.7, 8.83) * mm, "end": v(-7.28, 8.83) * mm});
            skLineSegment(sketch, "E26.5.2.0", {"start": v(-6.53, 6.63) * mm, "end": v(-6.35, 6.09) * mm});
            skLineSegment(sketch, "E26.5.2.1", {"start": v(-5.78, 6.09) * mm, "end": v(-6.35, 6.09) * mm});
            skLineSegment(sketch, "E26.5.2.2", {"start": v(-5.78, 6.09) * mm, "end": v(-6.24, 5.75) * mm});
            skLineSegment(sketch, "E26.5.2.3", {"start": v(-6.24, 5.75) * mm, "end": v(-6.06, 5.2) * mm});
            skLineSegment(sketch, "E26.5.2.4", {"start": v(-6.53, 5.54) * mm, "end": v(-6.06, 5.2) * mm});
            skLineSegment(sketch, "E26.5.2.5", {"start": v(-6.53, 5.54) * mm, "end": v(-7, 5.2) * mm});
            skLineSegment(sketch, "E26.5.2.6", {"start": v(-7, 5.2) * mm, "end": v(-6.81, 5.75) * mm});
            skLineSegment(sketch, "E26.5.2.7", {"start": v(-7.28, 6.09) * mm, "end": v(-6.81, 5.75) * mm});
            skLineSegment(sketch, "E26.5.2.8", {"start": v(-6.7, 6.09) * mm, "end": v(-6.53, 6.63) * mm});
            skLineSegment(sketch, "E26.5.2.9", {"start": v(-6.7, 6.09) * mm, "end": v(-7.28, 6.09) * mm});
            skLineSegment(sketch, "E26.5.3.0", {"start": v(-6.53, 3.89) * mm, "end": v(-6.35, 3.34) * mm});
            skLineSegment(sketch, "E26.5.3.1", {"start": v(-5.78, 3.34) * mm, "end": v(-6.35, 3.34) * mm});
            skLineSegment(sketch, "E26.5.3.2", {"start": v(-5.78, 3.34) * mm, "end": v(-6.24, 3) * mm});
            skLineSegment(sketch, "E26.5.3.3", {"start": v(-6.24, 3) * mm, "end": v(-6.06, 2.46) * mm});
            skLineSegment(sketch, "E26.5.3.4", {"start": v(-6.53, 2.8) * mm, "end": v(-6.06, 2.46) * mm});
            skLineSegment(sketch, "E26.5.3.5", {"start": v(-6.53, 2.8) * mm, "end": v(-7, 2.46) * mm});
            skLineSegment(sketch, "E26.5.3.6", {"start": v(-7, 2.46) * mm, "end": v(-6.81, 3) * mm});
            skLineSegment(sketch, "E26.5.3.7", {"start": v(-7.28, 3.34) * mm, "end": v(-6.81, 3) * mm});
            skLineSegment(sketch, "E26.5.3.8", {"start": v(-6.7, 3.34) * mm, "end": v(-6.53, 3.89) * mm});
            skLineSegment(sketch, "E26.5.3.9", {"start": v(-6.7, 3.34) * mm, "end": v(-7.28, 3.34) * mm});
            skLineSegment(sketch, "E26.5.4.0", {"start": v(-6.53, 1.14) * mm, "end": v(-6.35, 0.6) * mm});
            skLineSegment(sketch, "E26.5.4.1", {"start": v(-5.78, 0.6) * mm, "end": v(-6.35, 0.6) * mm});
            skLineSegment(sketch, "E26.5.4.2", {"start": v(-5.78, 0.6) * mm, "end": v(-6.24, 0.26) * mm});
            skLineSegment(sketch, "E26.5.4.3", {"start": v(-6.24, 0.26) * mm, "end": v(-6.06, -0.28) * mm});
            skLineSegment(sketch, "E26.5.4.4", {"start": v(-6.53, 0.05) * mm, "end": v(-6.06, -0.28) * mm});
            skLineSegment(sketch, "E26.5.4.5", {"start": v(-6.53, 0.05) * mm, "end": v(-7, -0.28) * mm});
            skLineSegment(sketch, "E26.5.4.6", {"start": v(-7, -0.28) * mm, "end": v(-6.81, 0.26) * mm});
            skLineSegment(sketch, "E26.5.4.7", {"start": v(-7.28, 0.6) * mm, "end": v(-6.81, 0.26) * mm});
            skLineSegment(sketch, "E26.5.4.8", {"start": v(-6.7, 0.6) * mm, "end": v(-6.53, 1.14) * mm});
            skLineSegment(sketch, "E26.5.4.9", {"start": v(-6.7, 0.6) * mm, "end": v(-7.28, 0.6) * mm});
            skLineSegment(sketch, "E26.direction1", {"start": v(-22.35, 11.57) * mm, "end": v(-19.15, 11.57) * mm, "construction": true});
            skLineSegment(sketch, "E26.direction2", {"start": v(-22.35, 11.57) * mm, "end": v(-22.35, 8.83) * mm, "construction": true});
            skPoint(sketch, "E27.cCircle.perimeterSnap0", {"position": v(-20.93, 10.64) * mm});
            skPoint(sketch, "E27.0.startSnap0", {"position": v(-20.93, 10.64) * mm});
            skLineSegment(sketch, "E28", {"start": v(-20.93, 10.75) * mm, "end": v(-20.75, 10.2) * mm});
            skLineSegment(sketch, "E29", {"start": v(-21.68, 10.2) * mm, "end": v(-21.1, 10.2) * mm});
            skLineSegment(sketch, "E30", {"start": v(-21.4, 9.32) * mm, "end": v(-20.93, 9.66) * mm});
            skLineSegment(sketch, "E31", {"start": v(-21.4, 9.32) * mm, "end": v(-21.22, 9.86) * mm});
            skLineSegment(sketch, "E32", {"start": v(-20.47, 9.32) * mm, "end": v(-20.93, 9.66) * mm});
            skLineSegment(sketch, "E33.trimOffspring", {"start": v(-20.64, 9.86) * mm, "end": v(-20.47, 9.32) * mm});
            skLineSegment(sketch, "E34.trimOffspring", {"start": v(-20.75, 10.2) * mm, "end": v(-20.18, 10.2) * mm});
            skLineSegment(sketch, "E35.trimOffspring", {"start": v(-21.1, 10.2) * mm, "end": v(-20.93, 10.75) * mm});
            skLineSegment(sketch, "E36.trimOffspring", {"start": v(-21.22, 9.86) * mm, "end": v(-21.68, 10.2) * mm});
            skLineSegment(sketch, "E37.trimOffspring", {"start": v(-20.64, 9.86) * mm, "end": v(-20.18, 10.2) * mm});
            skLineSegment(sketch, "E38.0.1.0", {"start": v(-20.93, 8) * mm, "end": v(-20.75, 7.46) * mm});
            skLineSegment(sketch, "E38.0.1.1", {"start": v(-20.75, 7.46) * mm, "end": v(-20.18, 7.46) * mm});
            skLineSegment(sketch, "E38.0.1.2", {"start": v(-20.64, 7.12) * mm, "end": v(-20.18, 7.46) * mm});
            skLineSegment(sketch, "E38.0.1.3", {"start": v(-20.64, 7.12) * mm, "end": v(-20.47, 6.57) * mm});
            skLineSegment(sketch, "E38.0.1.4", {"start": v(-20.47, 6.57) * mm, "end": v(-20.93, 6.91) * mm});
            skLineSegment(sketch, "E38.0.1.5", {"start": v(-21.4, 6.57) * mm, "end": v(-20.93, 6.91) * mm});
            skLineSegment(sketch, "E38.0.1.6", {"start": v(-21.4, 6.57) * mm, "end": v(-21.22, 7.12) * mm});
            skLineSegment(sketch, "E38.0.1.7", {"start": v(-21.22, 7.12) * mm, "end": v(-21.68, 7.46) * mm});
            skLineSegment(sketch, "E38.0.1.8", {"start": v(-21.68, 7.46) * mm, "end": v(-21.1, 7.46) * mm});
            skLineSegment(sketch, "E38.0.1.9", {"start": v(-21.1, 7.46) * mm, "end": v(-20.93, 8) * mm});
            skLineSegment(sketch, "E38.0.2.0", {"start": v(-20.93, 5.26) * mm, "end": v(-20.75, 4.71) * mm});
            skLineSegment(sketch, "E38.0.2.1", {"start": v(-20.75, 4.71) * mm, "end": v(-20.18, 4.71) * mm});
            skLineSegment(sketch, "E38.0.2.2", {"start": v(-20.64, 4.38) * mm, "end": v(-20.18, 4.71) * mm});
            skLineSegment(sketch, "E38.0.2.3", {"start": v(-20.64, 4.38) * mm, "end": v(-20.47, 3.83) * mm});
            skLineSegment(sketch, "E38.0.2.4", {"start": v(-20.47, 3.83) * mm, "end": v(-20.93, 4.17) * mm});
            skLineSegment(sketch, "E38.0.2.5", {"start": v(-21.4, 3.83) * mm, "end": v(-20.93, 4.17) * mm});
            skLineSegment(sketch, "E38.0.2.6", {"start": v(-21.4, 3.83) * mm, "end": v(-21.22, 4.38) * mm});
            skLineSegment(sketch, "E38.0.2.7", {"start": v(-21.22, 4.38) * mm, "end": v(-21.68, 4.71) * mm});
            skLineSegment(sketch, "E38.0.2.8", {"start": v(-21.68, 4.71) * mm, "end": v(-21.1, 4.71) * mm});
            skLineSegment(sketch, "E38.0.2.9", {"start": v(-21.1, 4.71) * mm, "end": v(-20.93, 5.26) * mm});
            skLineSegment(sketch, "E38.0.3.0", {"start": v(-20.93, 2.52) * mm, "end": v(-20.75, 1.97) * mm});
            skLineSegment(sketch, "E38.0.3.1", {"start": v(-20.75, 1.97) * mm, "end": v(-20.18, 1.97) * mm});
            skLineSegment(sketch, "E38.0.3.2", {"start": v(-20.64, 1.63) * mm, "end": v(-20.18, 1.97) * mm});
            skLineSegment(sketch, "E38.0.3.3", {"start": v(-20.64, 1.63) * mm, "end": v(-20.47, 1.09) * mm});
            skLineSegment(sketch, "E38.0.3.4", {"start": v(-20.47, 1.09) * mm, "end": v(-20.93, 1.43) * mm});
            skLineSegment(sketch, "E38.0.3.5", {"start": v(-21.4, 1.09) * mm, "end": v(-20.93, 1.43) * mm});
            skLineSegment(sketch, "E38.0.3.6", {"start": v(-21.4, 1.09) * mm, "end": v(-21.22, 1.63) * mm});
            skLineSegment(sketch, "E38.0.3.7", {"start": v(-21.22, 1.63) * mm, "end": v(-21.68, 1.97) * mm});
            skLineSegment(sketch, "E38.0.3.8", {"start": v(-21.68, 1.97) * mm, "end": v(-21.1, 1.97) * mm});
            skLineSegment(sketch, "E38.0.3.9", {"start": v(-21.1, 1.97) * mm, "end": v(-20.93, 2.52) * mm});
            skLineSegment(sketch, "E38.1.0.0", {"start": v(-17.73, 10.75) * mm, "end": v(-17.55, 10.2) * mm});
            skLineSegment(sketch, "E38.1.0.1", {"start": v(-17.55, 10.2) * mm, "end": v(-16.98, 10.2) * mm});
            skLineSegment(sketch, "E38.1.0.2", {"start": v(-17.44, 9.86) * mm, "end": v(-16.98, 10.2) * mm});
            skLineSegment(sketch, "E38.1.0.3", {"start": v(-17.44, 9.86) * mm, "end": v(-17.26, 9.32) * mm});
            skLineSegment(sketch, "E38.1.0.4", {"start": v(-17.26, 9.32) * mm, "end": v(-17.73, 9.66) * mm});
            skLineSegment(sketch, "E38.1.0.5", {"start": v(-18.2, 9.32) * mm, "end": v(-17.73, 9.66) * mm});
            skLineSegment(sketch, "E38.1.0.6", {"start": v(-18.2, 9.32) * mm, "end": v(-18.02, 9.86) * mm});
            skLineSegment(sketch, "E38.1.0.7", {"start": v(-18.02, 9.86) * mm, "end": v(-18.48, 10.2) * mm});
            skLineSegment(sketch, "E38.1.0.8", {"start": v(-18.48, 10.2) * mm, "end": v(-17.9, 10.2) * mm});
            skLineSegment(sketch, "E38.1.0.9", {"start": v(-17.9, 10.2) * mm, "end": v(-17.73, 10.75) * mm});
            skLineSegment(sketch, "E38.1.1.0", {"start": v(-17.73, 8) * mm, "end": v(-17.55, 7.46) * mm});
            skLineSegment(sketch, "E38.1.1.1", {"start": v(-17.55, 7.46) * mm, "end": v(-16.98, 7.46) * mm});
            skLineSegment(sketch, "E38.1.1.2", {"start": v(-17.44, 7.12) * mm, "end": v(-16.98, 7.46) * mm});
            skLineSegment(sketch, "E38.1.1.3", {"start": v(-17.44, 7.12) * mm, "end": v(-17.26, 6.57) * mm});
            skLineSegment(sketch, "E38.1.1.4", {"start": v(-17.26, 6.57) * mm, "end": v(-17.73, 6.91) * mm});
            skLineSegment(sketch, "E38.1.1.5", {"start": v(-18.2, 6.57) * mm, "end": v(-17.73, 6.91) * mm});
            skLineSegment(sketch, "E38.1.1.6", {"start": v(-18.2, 6.57) * mm, "end": v(-18.02, 7.12) * mm});
            skLineSegment(sketch, "E38.1.1.7", {"start": v(-18.02, 7.12) * mm, "end": v(-18.48, 7.46) * mm});
            skLineSegment(sketch, "E38.1.1.8", {"start": v(-18.48, 7.46) * mm, "end": v(-17.9, 7.46) * mm});
            skLineSegment(sketch, "E38.1.1.9", {"start": v(-17.9, 7.46) * mm, "end": v(-17.73, 8) * mm});
            skLineSegment(sketch, "E38.1.2.0", {"start": v(-17.73, 5.26) * mm, "end": v(-17.55, 4.71) * mm});
            skLineSegment(sketch, "E38.1.2.1", {"start": v(-17.55, 4.71) * mm, "end": v(-16.98, 4.71) * mm});
            skLineSegment(sketch, "E38.1.2.2", {"start": v(-17.44, 4.38) * mm, "end": v(-16.98, 4.71) * mm});
            skLineSegment(sketch, "E38.1.2.3", {"start": v(-17.44, 4.38) * mm, "end": v(-17.26, 3.83) * mm});
            skLineSegment(sketch, "E38.1.2.4", {"start": v(-17.26, 3.83) * mm, "end": v(-17.73, 4.17) * mm});
            skLineSegment(sketch, "E38.1.2.5", {"start": v(-18.2, 3.83) * mm, "end": v(-17.73, 4.17) * mm});
            skLineSegment(sketch, "E38.1.2.6", {"start": v(-18.2, 3.83) * mm, "end": v(-18.02, 4.38) * mm});
            skLineSegment(sketch, "E38.1.2.7", {"start": v(-18.02, 4.38) * mm, "end": v(-18.48, 4.71) * mm});
            skLineSegment(sketch, "E38.1.2.8", {"start": v(-18.48, 4.71) * mm, "end": v(-17.9, 4.71) * mm});
            skLineSegment(sketch, "E38.1.2.9", {"start": v(-17.9, 4.71) * mm, "end": v(-17.73, 5.26) * mm});
            skLineSegment(sketch, "E38.1.3.0", {"start": v(-17.73, 2.52) * mm, "end": v(-17.55, 1.97) * mm});
            skLineSegment(sketch, "E38.1.3.1", {"start": v(-17.55, 1.97) * mm, "end": v(-16.98, 1.97) * mm});
            skLineSegment(sketch, "E38.1.3.2", {"start": v(-17.44, 1.63) * mm, "end": v(-16.98, 1.97) * mm});
            skLineSegment(sketch, "E38.1.3.3", {"start": v(-17.44, 1.63) * mm, "end": v(-17.26, 1.09) * mm});
            skLineSegment(sketch, "E38.1.3.4", {"start": v(-17.26, 1.09) * mm, "end": v(-17.73, 1.43) * mm});
            skLineSegment(sketch, "E38.1.3.5", {"start": v(-18.2, 1.09) * mm, "end": v(-17.73, 1.43) * mm});
            skLineSegment(sketch, "E38.1.3.6", {"start": v(-18.2, 1.09) * mm, "end": v(-18.02, 1.63) * mm});
            skLineSegment(sketch, "E38.1.3.7", {"start": v(-18.02, 1.63) * mm, "end": v(-18.48, 1.97) * mm});
            skLineSegment(sketch, "E38.1.3.8", {"start": v(-18.48, 1.97) * mm, "end": v(-17.9, 1.97) * mm});
            skLineSegment(sketch, "E38.1.3.9", {"start": v(-17.9, 1.97) * mm, "end": v(-17.73, 2.52) * mm});
            skLineSegment(sketch, "E38.2.0.0", {"start": v(-14.53, 10.75) * mm, "end": v(-14.35, 10.2) * mm});
            skLineSegment(sketch, "E38.2.0.1", {"start": v(-14.35, 10.2) * mm, "end": v(-13.78, 10.2) * mm});
            skLineSegment(sketch, "E38.2.0.2", {"start": v(-14.24, 9.86) * mm, "end": v(-13.78, 10.2) * mm});
            skLineSegment(sketch, "E38.2.0.3", {"start": v(-14.24, 9.86) * mm, "end": v(-14.06, 9.32) * mm});
            skLineSegment(sketch, "E38.2.0.4", {"start": v(-14.06, 9.32) * mm, "end": v(-14.53, 9.66) * mm});
            skLineSegment(sketch, "E38.2.0.5", {"start": v(-15, 9.32) * mm, "end": v(-14.53, 9.66) * mm});
            skLineSegment(sketch, "E38.2.0.6", {"start": v(-15, 9.32) * mm, "end": v(-14.82, 9.86) * mm});
            skLineSegment(sketch, "E38.2.0.7", {"start": v(-14.82, 9.86) * mm, "end": v(-15.28, 10.2) * mm});
            skLineSegment(sketch, "E38.2.0.8", {"start": v(-15.28, 10.2) * mm, "end": v(-14.7, 10.2) * mm});
            skLineSegment(sketch, "E38.2.0.9", {"start": v(-14.7, 10.2) * mm, "end": v(-14.53, 10.75) * mm});
            skLineSegment(sketch, "E38.2.1.0", {"start": v(-14.53, 8) * mm, "end": v(-14.35, 7.46) * mm});
            skLineSegment(sketch, "E38.2.1.1", {"start": v(-14.35, 7.46) * mm, "end": v(-13.78, 7.46) * mm});
            skLineSegment(sketch, "E38.2.1.2", {"start": v(-14.24, 7.12) * mm, "end": v(-13.78, 7.46) * mm});
            skLineSegment(sketch, "E38.2.1.3", {"start": v(-14.24, 7.12) * mm, "end": v(-14.06, 6.57) * mm});
            skLineSegment(sketch, "E38.2.1.4", {"start": v(-14.06, 6.57) * mm, "end": v(-14.53, 6.91) * mm});
            skLineSegment(sketch, "E38.2.1.5", {"start": v(-15, 6.57) * mm, "end": v(-14.53, 6.91) * mm});
            skLineSegment(sketch, "E38.2.1.6", {"start": v(-15, 6.57) * mm, "end": v(-14.82, 7.12) * mm});
            skLineSegment(sketch, "E38.2.1.7", {"start": v(-14.82, 7.12) * mm, "end": v(-15.28, 7.46) * mm});
            skLineSegment(sketch, "E38.2.1.8", {"start": v(-15.28, 7.46) * mm, "end": v(-14.7, 7.46) * mm});
            skLineSegment(sketch, "E38.2.1.9", {"start": v(-14.7, 7.46) * mm, "end": v(-14.53, 8) * mm});
            skLineSegment(sketch, "E38.2.2.0", {"start": v(-14.53, 5.26) * mm, "end": v(-14.35, 4.71) * mm});
            skLineSegment(sketch, "E38.2.2.1", {"start": v(-14.35, 4.71) * mm, "end": v(-13.78, 4.71) * mm});
            skLineSegment(sketch, "E38.2.2.2", {"start": v(-14.24, 4.38) * mm, "end": v(-13.78, 4.71) * mm});
            skLineSegment(sketch, "E38.2.2.3", {"start": v(-14.24, 4.38) * mm, "end": v(-14.06, 3.83) * mm});
            skLineSegment(sketch, "E38.2.2.4", {"start": v(-14.06, 3.83) * mm, "end": v(-14.53, 4.17) * mm});
            skLineSegment(sketch, "E38.2.2.5", {"start": v(-15, 3.83) * mm, "end": v(-14.53, 4.17) * mm});
            skLineSegment(sketch, "E38.2.2.6", {"start": v(-15, 3.83) * mm, "end": v(-14.82, 4.38) * mm});
            skLineSegment(sketch, "E38.2.2.7", {"start": v(-14.82, 4.38) * mm, "end": v(-15.28, 4.71) * mm});
            skLineSegment(sketch, "E38.2.2.8", {"start": v(-15.28, 4.71) * mm, "end": v(-14.7, 4.71) * mm});
            skLineSegment(sketch, "E38.2.2.9", {"start": v(-14.7, 4.71) * mm, "end": v(-14.53, 5.26) * mm});
            skLineSegment(sketch, "E38.2.3.0", {"start": v(-14.53, 2.52) * mm, "end": v(-14.35, 1.97) * mm});
            skLineSegment(sketch, "E38.2.3.1", {"start": v(-14.35, 1.97) * mm, "end": v(-13.78, 1.97) * mm});
            skLineSegment(sketch, "E38.2.3.2", {"start": v(-14.24, 1.63) * mm, "end": v(-13.78, 1.97) * mm});
            skLineSegment(sketch, "E38.2.3.3", {"start": v(-14.24, 1.63) * mm, "end": v(-14.06, 1.09) * mm});
            skLineSegment(sketch, "E38.2.3.4", {"start": v(-14.06, 1.09) * mm, "end": v(-14.53, 1.43) * mm});
            skLineSegment(sketch, "E38.2.3.5", {"start": v(-15, 1.09) * mm, "end": v(-14.53, 1.43) * mm});
            skLineSegment(sketch, "E38.2.3.6", {"start": v(-15, 1.09) * mm, "end": v(-14.82, 1.63) * mm});
            skLineSegment(sketch, "E38.2.3.7", {"start": v(-14.82, 1.63) * mm, "end": v(-15.28, 1.97) * mm});
            skLineSegment(sketch, "E38.2.3.8", {"start": v(-15.28, 1.97) * mm, "end": v(-14.7, 1.97) * mm});
            skLineSegment(sketch, "E38.2.3.9", {"start": v(-14.7, 1.97) * mm, "end": v(-14.53, 2.52) * mm});
            skLineSegment(sketch, "E38.3.0.0", {"start": v(-11.33, 10.75) * mm, "end": v(-11.15, 10.2) * mm});
            skLineSegment(sketch, "E38.3.0.1", {"start": v(-11.15, 10.2) * mm, "end": v(-10.58, 10.2) * mm});
            skLineSegment(sketch, "E38.3.0.2", {"start": v(-11.04, 9.86) * mm, "end": v(-10.58, 10.2) * mm});
            skLineSegment(sketch, "E38.3.0.3", {"start": v(-11.04, 9.86) * mm, "end": v(-10.86, 9.32) * mm});
            skLineSegment(sketch, "E38.3.0.4", {"start": v(-10.86, 9.32) * mm, "end": v(-11.33, 9.66) * mm});
            skLineSegment(sketch, "E38.3.0.5", {"start": v(-11.8, 9.32) * mm, "end": v(-11.33, 9.66) * mm});
            skLineSegment(sketch, "E38.3.0.6", {"start": v(-11.8, 9.32) * mm, "end": v(-11.62, 9.86) * mm});
            skLineSegment(sketch, "E38.3.0.7", {"start": v(-11.62, 9.86) * mm, "end": v(-12.08, 10.2) * mm});
            skLineSegment(sketch, "E38.3.0.8", {"start": v(-12.08, 10.2) * mm, "end": v(-11.5, 10.2) * mm});
            skLineSegment(sketch, "E38.3.0.9", {"start": v(-11.5, 10.2) * mm, "end": v(-11.33, 10.75) * mm});
            skLineSegment(sketch, "E38.3.1.0", {"start": v(-11.33, 8) * mm, "end": v(-11.15, 7.46) * mm});
            skLineSegment(sketch, "E38.3.1.1", {"start": v(-11.15, 7.46) * mm, "end": v(-10.58, 7.46) * mm});
            skLineSegment(sketch, "E38.3.1.2", {"start": v(-11.04, 7.12) * mm, "end": v(-10.58, 7.46) * mm});
            skLineSegment(sketch, "E38.3.1.3", {"start": v(-11.04, 7.12) * mm, "end": v(-10.86, 6.57) * mm});
            skLineSegment(sketch, "E38.3.1.4", {"start": v(-10.86, 6.57) * mm, "end": v(-11.33, 6.91) * mm});
            skLineSegment(sketch, "E38.3.1.5", {"start": v(-11.8, 6.57) * mm, "end": v(-11.33, 6.91) * mm});
            skLineSegment(sketch, "E38.3.1.6", {"start": v(-11.8, 6.57) * mm, "end": v(-11.62, 7.12) * mm});
            skLineSegment(sketch, "E38.3.1.7", {"start": v(-11.62, 7.12) * mm, "end": v(-12.08, 7.46) * mm});
            skLineSegment(sketch, "E38.3.1.8", {"start": v(-12.08, 7.46) * mm, "end": v(-11.5, 7.46) * mm});
            skLineSegment(sketch, "E38.3.1.9", {"start": v(-11.5, 7.46) * mm, "end": v(-11.33, 8) * mm});
            skLineSegment(sketch, "E38.3.2.0", {"start": v(-11.33, 5.26) * mm, "end": v(-11.15, 4.71) * mm});
            skLineSegment(sketch, "E38.3.2.1", {"start": v(-11.15, 4.71) * mm, "end": v(-10.58, 4.71) * mm});
            skLineSegment(sketch, "E38.3.2.2", {"start": v(-11.04, 4.38) * mm, "end": v(-10.58, 4.71) * mm});
            skLineSegment(sketch, "E38.3.2.3", {"start": v(-11.04, 4.38) * mm, "end": v(-10.86, 3.83) * mm});
            skLineSegment(sketch, "E38.3.2.4", {"start": v(-10.86, 3.83) * mm, "end": v(-11.33, 4.17) * mm});
            skLineSegment(sketch, "E38.3.2.5", {"start": v(-11.8, 3.83) * mm, "end": v(-11.33, 4.17) * mm});
            skLineSegment(sketch, "E38.3.2.6", {"start": v(-11.8, 3.83) * mm, "end": v(-11.62, 4.38) * mm});
            skLineSegment(sketch, "E38.3.2.7", {"start": v(-11.62, 4.38) * mm, "end": v(-12.08, 4.71) * mm});
            skLineSegment(sketch, "E38.3.2.8", {"start": v(-12.08, 4.71) * mm, "end": v(-11.5, 4.71) * mm});
            skLineSegment(sketch, "E38.3.2.9", {"start": v(-11.5, 4.71) * mm, "end": v(-11.33, 5.26) * mm});
            skLineSegment(sketch, "E38.3.3.0", {"start": v(-11.33, 2.52) * mm, "end": v(-11.15, 1.97) * mm});
            skLineSegment(sketch, "E38.3.3.1", {"start": v(-11.15, 1.97) * mm, "end": v(-10.58, 1.97) * mm});
            skLineSegment(sketch, "E38.3.3.2", {"start": v(-11.04, 1.63) * mm, "end": v(-10.58, 1.97) * mm});
            skLineSegment(sketch, "E38.3.3.3", {"start": v(-11.04, 1.63) * mm, "end": v(-10.86, 1.09) * mm});
            skLineSegment(sketch, "E38.3.3.4", {"start": v(-10.86, 1.09) * mm, "end": v(-11.33, 1.43) * mm});
            skLineSegment(sketch, "E38.3.3.5", {"start": v(-11.8, 1.09) * mm, "end": v(-11.33, 1.43) * mm});
            skLineSegment(sketch, "E38.3.3.6", {"start": v(-11.8, 1.09) * mm, "end": v(-11.62, 1.63) * mm});
            skLineSegment(sketch, "E38.3.3.7", {"start": v(-11.62, 1.63) * mm, "end": v(-12.08, 1.97) * mm});
            skLineSegment(sketch, "E38.3.3.8", {"start": v(-12.08, 1.97) * mm, "end": v(-11.5, 1.97) * mm});
            skLineSegment(sketch, "E38.3.3.9", {"start": v(-11.5, 1.97) * mm, "end": v(-11.33, 2.52) * mm});
            skLineSegment(sketch, "E38.4.0.0", {"start": v(-8.13, 10.75) * mm, "end": v(-7.95, 10.2) * mm});
            skLineSegment(sketch, "E38.4.0.1", {"start": v(-7.95, 10.2) * mm, "end": v(-7.38, 10.2) * mm});
            skLineSegment(sketch, "E38.4.0.2", {"start": v(-7.84, 9.86) * mm, "end": v(-7.38, 10.2) * mm});
            skLineSegment(sketch, "E38.4.0.3", {"start": v(-7.84, 9.86) * mm, "end": v(-7.66, 9.32) * mm});
            skLineSegment(sketch, "E38.4.0.4", {"start": v(-7.66, 9.32) * mm, "end": v(-8.13, 9.66) * mm});
            skLineSegment(sketch, "E38.4.0.5", {"start": v(-8.6, 9.32) * mm, "end": v(-8.13, 9.66) * mm});
            skLineSegment(sketch, "E38.4.0.6", {"start": v(-8.6, 9.32) * mm, "end": v(-8.41, 9.86) * mm});
            skLineSegment(sketch, "E38.4.0.7", {"start": v(-8.41, 9.86) * mm, "end": v(-8.88, 10.2) * mm});
            skLineSegment(sketch, "E38.4.0.8", {"start": v(-8.88, 10.2) * mm, "end": v(-8.3, 10.2) * mm});
            skLineSegment(sketch, "E38.4.0.9", {"start": v(-8.3, 10.2) * mm, "end": v(-8.13, 10.75) * mm});
            skLineSegment(sketch, "E38.4.1.0", {"start": v(-8.13, 8) * mm, "end": v(-7.95, 7.46) * mm});
            skLineSegment(sketch, "E38.4.1.1", {"start": v(-7.95, 7.46) * mm, "end": v(-7.38, 7.46) * mm});
            skLineSegment(sketch, "E38.4.1.2", {"start": v(-7.84, 7.12) * mm, "end": v(-7.38, 7.46) * mm});
            skLineSegment(sketch, "E38.4.1.3", {"start": v(-7.84, 7.12) * mm, "end": v(-7.66, 6.57) * mm});
            skLineSegment(sketch, "E38.4.1.4", {"start": v(-7.66, 6.57) * mm, "end": v(-8.13, 6.91) * mm});
            skLineSegment(sketch, "E38.4.1.5", {"start": v(-8.6, 6.57) * mm, "end": v(-8.13, 6.91) * mm});
            skLineSegment(sketch, "E38.4.1.6", {"start": v(-8.6, 6.57) * mm, "end": v(-8.41, 7.12) * mm});
            skLineSegment(sketch, "E38.4.1.7", {"start": v(-8.41, 7.12) * mm, "end": v(-8.88, 7.46) * mm});
            skLineSegment(sketch, "E38.4.1.8", {"start": v(-8.88, 7.46) * mm, "end": v(-8.3, 7.46) * mm});
            skLineSegment(sketch, "E38.4.1.9", {"start": v(-8.3, 7.46) * mm, "end": v(-8.13, 8) * mm});
            skLineSegment(sketch, "E38.4.2.0", {"start": v(-8.13, 5.26) * mm, "end": v(-7.95, 4.71) * mm});
            skLineSegment(sketch, "E38.4.2.1", {"start": v(-7.95, 4.71) * mm, "end": v(-7.38, 4.71) * mm});
            skLineSegment(sketch, "E38.4.2.2", {"start": v(-7.84, 4.38) * mm, "end": v(-7.38, 4.71) * mm});
            skLineSegment(sketch, "E38.4.2.3", {"start": v(-7.84, 4.38) * mm, "end": v(-7.66, 3.83) * mm});
            skLineSegment(sketch, "E38.4.2.4", {"start": v(-7.66, 3.83) * mm, "end": v(-8.13, 4.17) * mm});
            skLineSegment(sketch, "E38.4.2.5", {"start": v(-8.6, 3.83) * mm, "end": v(-8.13, 4.17) * mm});
            skLineSegment(sketch, "E38.4.2.6", {"start": v(-8.6, 3.83) * mm, "end": v(-8.41, 4.38) * mm});
            skLineSegment(sketch, "E38.4.2.7", {"start": v(-8.41, 4.38) * mm, "end": v(-8.88, 4.71) * mm});
            skLineSegment(sketch, "E38.4.2.8", {"start": v(-8.88, 4.71) * mm, "end": v(-8.3, 4.71) * mm});
            skLineSegment(sketch, "E38.4.2.9", {"start": v(-8.3, 4.71) * mm, "end": v(-8.13, 5.26) * mm});
            skLineSegment(sketch, "E38.4.3.0", {"start": v(-8.13, 2.52) * mm, "end": v(-7.95, 1.97) * mm});
            skLineSegment(sketch, "E38.4.3.1", {"start": v(-7.95, 1.97) * mm, "end": v(-7.38, 1.97) * mm});
            skLineSegment(sketch, "E38.4.3.2", {"start": v(-7.84, 1.63) * mm, "end": v(-7.38, 1.97) * mm});
            skLineSegment(sketch, "E38.4.3.3", {"start": v(-7.84, 1.63) * mm, "end": v(-7.66, 1.09) * mm});
            skLineSegment(sketch, "E38.4.3.4", {"start": v(-7.66, 1.09) * mm, "end": v(-8.13, 1.43) * mm});
            skLineSegment(sketch, "E38.4.3.5", {"start": v(-8.6, 1.09) * mm, "end": v(-8.13, 1.43) * mm});
            skLineSegment(sketch, "E38.4.3.6", {"start": v(-8.6, 1.09) * mm, "end": v(-8.41, 1.63) * mm});
            skLineSegment(sketch, "E38.4.3.7", {"start": v(-8.41, 1.63) * mm, "end": v(-8.88, 1.97) * mm});
            skLineSegment(sketch, "E38.4.3.8", {"start": v(-8.88, 1.97) * mm, "end": v(-8.3, 1.97) * mm});
            skLineSegment(sketch, "E38.4.3.9", {"start": v(-8.3, 1.97) * mm, "end": v(-8.13, 2.52) * mm});
            skLineSegment(sketch, "E38.direction1", {"start": v(-20.75, 10.2) * mm, "end": v(-17.55, 10.2) * mm, "construction": true});
            skLineSegment(sketch, "E38.direction2", {"start": v(-20.75, 10.2) * mm, "end": v(-20.75, 7.46) * mm, "construction": true});
            skSolve(sketch);
        }
        {
            var Q0;
            Q0=makeQuery(id+"F0.imprint","IMPRINT",FACE,{"disambiguationData":[TD([[makeQuery(id+"F0.imprint","IMPRINT",EDGE,{"derivedFrom":sQuery(id+"F0.wireOp",EDGE,"E16")}),-1.0]])]});
            var Q1;
            Q1=makeQuery(id+"F0.imprint","IMPRINT",FACE,{"disambiguationData":[TD([[makeQuery(id+"F0.imprint","IMPRINT",EDGE,{"derivedFrom":sQuery(id+"F0.wireOp",EDGE,"E26.0.1.0")}),-1.0]])]});
            var Q2;
            Q2=makeQuery(id+"F0.imprint","IMPRINT",FACE,{"disambiguationData":[TD([[makeQuery(id+"F0.imprint","IMPRINT",EDGE,{"derivedFrom":sQuery(id+"F0.wireOp",EDGE,"E28")}),-1.0]])]});
            var Q3;
            Q3=makeQuery(id+"F0.imprint","IMPRINT",FACE,{"disambiguationData":[TD([[makeQuery(id+"F0.imprint","IMPRINT",EDGE,{"derivedFrom":sQuery(id+"F0.wireOp",EDGE,"E26.1.0.0")}),-1.0]])]});
            var Q4;
            Q4=makeQuery(id+"F0.imprint","IMPRINT",FACE,{"disambiguationData":[TD([[makeQuery(id+"F0.imprint","IMPRINT",EDGE,{"derivedFrom":sQuery(id+"F0.wireOp",EDGE,"E26.2.0.0")}),-1.0]])]});
            var Q5;
            Q5=makeQuery(id+"F0.imprint","IMPRINT",FACE,{"disambiguationData":[TD([[makeQuery(id+"F0.imprint","IMPRINT",EDGE,{"derivedFrom":sQuery(id+"F0.wireOp",EDGE,"E26.0.2.0")}),-1.0]])]});
            var Q6;
            Q6=makeQuery(id+"F0.imprint","IMPRINT",FACE,{"disambiguationData":[TD([[makeQuery(id+"F0.imprint","IMPRINT",EDGE,{"derivedFrom":sQuery(id+"F0.wireOp",EDGE,"E38.0.1.0")}),-1.0]])]});
            var Q7;
            Q7=makeQuery(id+"F0.imprint","IMPRINT",FACE,{"disambiguationData":[TD([[makeQuery(id+"F0.imprint","IMPRINT",EDGE,{"derivedFrom":sQuery(id+"F0.wireOp",EDGE,"E26.1.1.0")}),-1.0]])]});
            var Q8;
            Q8=makeQuery(id+"F0.imprint","IMPRINT",FACE,{"disambiguationData":[TD([[makeQuery(id+"F0.imprint","IMPRINT",EDGE,{"derivedFrom":sQuery(id+"F0.wireOp",EDGE,"E38.1.0.0")}),-1.0]])]});
            var Q9;
            Q9=makeQuery(id+"F0.imprint","IMPRINT",FACE,{"disambiguationData":[TD([[makeQuery(id+"F0.imprint","IMPRINT",EDGE,{"derivedFrom":sQuery(id+"F0.wireOp",EDGE,"E26.3.0.0")}),-1.0]])]});
            var Q10;
            Q10=makeQuery(id+"F0.imprint","IMPRINT",FACE,{"disambiguationData":[TD([[makeQuery(id+"F0.imprint","IMPRINT",EDGE,{"derivedFrom":sQuery(id+"F0.wireOp",EDGE,"E38.2.0.0")}),-1.0]])]});
            var Q11;
            Q11=makeQuery(id+"F0.imprint","IMPRINT",FACE,{"disambiguationData":[TD([[makeQuery(id+"F0.imprint","IMPRINT",EDGE,{"derivedFrom":sQuery(id+"F0.wireOp",EDGE,"E26.2.1.0")}),-1.0]])]});
            var Q12;
            Q12=makeQuery(id+"F0.imprint","IMPRINT",FACE,{"disambiguationData":[TD([[makeQuery(id+"F0.imprint","IMPRINT",EDGE,{"derivedFrom":sQuery(id+"F0.wireOp",EDGE,"E38.1.1.0")}),-1.0]])]});
            var Q13;
            Q13=makeQuery(id+"F0.imprint","IMPRINT",FACE,{"disambiguationData":[TD([[makeQuery(id+"F0.imprint","IMPRINT",EDGE,{"derivedFrom":sQuery(id+"F0.wireOp",EDGE,"E26.1.2.0")}),-1.0]])]});
            var Q14;
            Q14=makeQuery(id+"F0.imprint","IMPRINT",FACE,{"disambiguationData":[TD([[makeQuery(id+"F0.imprint","IMPRINT",EDGE,{"derivedFrom":sQuery(id+"F0.wireOp",EDGE,"E38.0.2.0")}),-1.0]])]});
            var Q15;
            Q15=makeQuery(id+"F0.imprint","IMPRINT",FACE,{"disambiguationData":[TD([[makeQuery(id+"F0.imprint","IMPRINT",EDGE,{"derivedFrom":sQuery(id+"F0.wireOp",EDGE,"E26.0.3.0")}),-1.0]])]});
            var Q16;
            Q16=makeQuery(id+"F0.imprint","IMPRINT",FACE,{"disambiguationData":[TD([[makeQuery(id+"F0.imprint","IMPRINT",EDGE,{"derivedFrom":sQuery(id+"F0.wireOp",EDGE,"E26.0.4.0")}),-1.0]])]});
            var Q17;
            Q17=makeQuery(id+"F0.imprint","IMPRINT",FACE,{"disambiguationData":[TD([[makeQuery(id+"F0.imprint","IMPRINT",EDGE,{"derivedFrom":sQuery(id+"F0.wireOp",EDGE,"E38.0.3.0")}),-1.0]])]});
            var Q18;
            Q18=makeQuery(id+"F0.imprint","IMPRINT",FACE,{"disambiguationData":[TD([[makeQuery(id+"F0.imprint","IMPRINT",EDGE,{"derivedFrom":sQuery(id+"F0.wireOp",EDGE,"E26.1.3.0")}),-1.0]])]});
            var Q19;
            Q19=makeQuery(id+"F0.imprint","IMPRINT",FACE,{"disambiguationData":[TD([[makeQuery(id+"F0.imprint","IMPRINT",EDGE,{"derivedFrom":sQuery(id+"F0.wireOp",EDGE,"E38.1.2.0")}),-1.0]])]});
            var Q20;
            Q20=makeQuery(id+"F0.imprint","IMPRINT",FACE,{"disambiguationData":[TD([[makeQuery(id+"F0.imprint","IMPRINT",EDGE,{"derivedFrom":sQuery(id+"F0.wireOp",EDGE,"E26.2.2.0")}),-1.0]])]});
            var Q21;
            Q21=makeQuery(id+"F0.imprint","IMPRINT",FACE,{"disambiguationData":[TD([[makeQuery(id+"F0.imprint","IMPRINT",EDGE,{"derivedFrom":sQuery(id+"F0.wireOp",EDGE,"E38.2.1.0")}),-1.0]])]});
            var Q22;
            Q22=makeQuery(id+"F0.imprint","IMPRINT",FACE,{"disambiguationData":[TD([[makeQuery(id+"F0.imprint","IMPRINT",EDGE,{"derivedFrom":sQuery(id+"F0.wireOp",EDGE,"E26.3.1.0")}),-1.0]])]});
            var Q23;
            Q23=makeQuery(id+"F0.imprint","IMPRINT",FACE,{"disambiguationData":[TD([[makeQuery(id+"F0.imprint","IMPRINT",EDGE,{"derivedFrom":sQuery(id+"F0.wireOp",EDGE,"E38.3.0.0")}),-1.0]])]});
            var Q24;
            Q24=makeQuery(id+"F0.imprint","IMPRINT",FACE,{"disambiguationData":[TD([[makeQuery(id+"F0.imprint","IMPRINT",EDGE,{"derivedFrom":sQuery(id+"F0.wireOp",EDGE,"E26.4.0.0")}),-1.0]])]});
            var Q25;
            Q25=makeQuery(id+"F0.imprint","IMPRINT",FACE,{"disambiguationData":[TD([[makeQuery(id+"F0.imprint","IMPRINT",EDGE,{"derivedFrom":sQuery(id+"F0.wireOp",EDGE,"E26.5.0.0")}),-1.0]])]});
            var Q26;
            Q26=makeQuery(id+"F0.imprint","IMPRINT",FACE,{"disambiguationData":[TD([[makeQuery(id+"F0.imprint","IMPRINT",EDGE,{"derivedFrom":sQuery(id+"F0.wireOp",EDGE,"E38.4.0.0")}),-1.0]])]});
            var Q27;
            Q27=makeQuery(id+"F0.imprint","IMPRINT",FACE,{"disambiguationData":[TD([[makeQuery(id+"F0.imprint","IMPRINT",EDGE,{"derivedFrom":sQuery(id+"F0.wireOp",EDGE,"E26.4.1.0")}),-1.0]])]});
            var Q28;
            Q28=makeQuery(id+"F0.imprint","IMPRINT",FACE,{"disambiguationData":[TD([[makeQuery(id+"F0.imprint","IMPRINT",EDGE,{"derivedFrom":sQuery(id+"F0.wireOp",EDGE,"E38.3.1.0")}),-1.0]])]});
            var Q29;
            Q29=makeQuery(id+"F0.imprint","IMPRINT",FACE,{"disambiguationData":[TD([[makeQuery(id+"F0.imprint","IMPRINT",EDGE,{"derivedFrom":sQuery(id+"F0.wireOp",EDGE,"E26.3.2.0")}),-1.0]])]});
            var Q30;
            Q30=makeQuery(id+"F0.imprint","IMPRINT",FACE,{"disambiguationData":[TD([[makeQuery(id+"F0.imprint","IMPRINT",EDGE,{"derivedFrom":sQuery(id+"F0.wireOp",EDGE,"E38.2.2.0")}),-1.0]])]});
            var Q31;
            Q31=makeQuery(id+"F0.imprint","IMPRINT",FACE,{"disambiguationData":[TD([[makeQuery(id+"F0.imprint","IMPRINT",EDGE,{"derivedFrom":sQuery(id+"F0.wireOp",EDGE,"E26.2.3.0")}),-1.0]])]});
            var Q32;
            Q32=makeQuery(id+"F0.imprint","IMPRINT",FACE,{"disambiguationData":[TD([[makeQuery(id+"F0.imprint","IMPRINT",EDGE,{"derivedFrom":sQuery(id+"F0.wireOp",EDGE,"E38.1.3.0")}),-1.0]])]});
            var Q33;
            Q33=makeQuery(id+"F0.imprint","IMPRINT",FACE,{"disambiguationData":[TD([[makeQuery(id+"F0.imprint","IMPRINT",EDGE,{"derivedFrom":sQuery(id+"F0.wireOp",EDGE,"E26.1.4.0")}),-1.0]])]});
            var Q34;
            Q34=makeQuery(id+"F0.imprint","IMPRINT",FACE,{"disambiguationData":[TD([[makeQuery(id+"F0.imprint","IMPRINT",EDGE,{"derivedFrom":sQuery(id+"F0.wireOp",EDGE,"E26.2.4.0")}),-1.0]])]});
            var Q35;
            Q35=makeQuery(id+"F0.imprint","IMPRINT",FACE,{"disambiguationData":[TD([[makeQuery(id+"F0.imprint","IMPRINT",EDGE,{"derivedFrom":sQuery(id+"F0.wireOp",EDGE,"E38.2.3.0")}),-1.0]])]});
            var Q36;
            Q36=makeQuery(id+"F0.imprint","IMPRINT",FACE,{"disambiguationData":[TD([[makeQuery(id+"F0.imprint","IMPRINT",EDGE,{"derivedFrom":sQuery(id+"F0.wireOp",EDGE,"E26.3.3.0")}),-1.0]])]});
            var Q37;
            Q37=makeQuery(id+"F0.imprint","IMPRINT",FACE,{"disambiguationData":[TD([[makeQuery(id+"F0.imprint","IMPRINT",EDGE,{"derivedFrom":sQuery(id+"F0.wireOp",EDGE,"E38.3.2.0")}),-1.0]])]});
            var Q38;
            Q38=makeQuery(id+"F0.imprint","IMPRINT",FACE,{"disambiguationData":[TD([[makeQuery(id+"F0.imprint","IMPRINT",EDGE,{"derivedFrom":sQuery(id+"F0.wireOp",EDGE,"E26.4.2.0")}),-1.0]])]});
            var Q39;
            Q39=makeQuery(id+"F0.imprint","IMPRINT",FACE,{"disambiguationData":[TD([[makeQuery(id+"F0.imprint","IMPRINT",EDGE,{"derivedFrom":sQuery(id+"F0.wireOp",EDGE,"E38.4.1.0")}),-1.0]])]});
            var Q40;
            Q40=makeQuery(id+"F0.imprint","IMPRINT",FACE,{"disambiguationData":[TD([[makeQuery(id+"F0.imprint","IMPRINT",EDGE,{"derivedFrom":sQuery(id+"F0.wireOp",EDGE,"E38.4.2.0")}),-1.0]])]});
            var Q41;
            Q41=makeQuery(id+"F0.imprint","IMPRINT",FACE,{"disambiguationData":[TD([[makeQuery(id+"F0.imprint","IMPRINT",EDGE,{"derivedFrom":sQuery(id+"F0.wireOp",EDGE,"E26.4.3.0")}),-1.0]])]});
            var Q42;
            Q42=makeQuery(id+"F0.imprint","IMPRINT",FACE,{"disambiguationData":[TD([[makeQuery(id+"F0.imprint","IMPRINT",EDGE,{"derivedFrom":sQuery(id+"F0.wireOp",EDGE,"E38.3.3.0")}),-1.0]])]});
            var Q43;
            Q43=makeQuery(id+"F0.imprint","IMPRINT",FACE,{"disambiguationData":[TD([[makeQuery(id+"F0.imprint","IMPRINT",EDGE,{"derivedFrom":sQuery(id+"F0.wireOp",EDGE,"E26.3.4.0")}),-1.0]])]});
            var Q44;
            Q44=makeQuery(id+"F0.imprint","IMPRINT",FACE,{"disambiguationData":[TD([[makeQuery(id+"F0.imprint","IMPRINT",EDGE,{"derivedFrom":sQuery(id+"F0.wireOp",EDGE,"E38.4.3.0")}),-1.0]])]});
            var Q45;
            Q45=makeQuery(id+"F0.imprint","IMPRINT",FACE,{"disambiguationData":[TD([[makeQuery(id+"F0.imprint","IMPRINT",EDGE,{"derivedFrom":sQuery(id+"F0.wireOp",EDGE,"E26.5.3.0")}),-1.0]])]});
            var Q46;
            Q46=makeQuery(id+"F0.imprint","IMPRINT",FACE,{"disambiguationData":[TD([[makeQuery(id+"F0.imprint","IMPRINT",EDGE,{"derivedFrom":sQuery(id+"F0.wireOp",EDGE,"E26.5.4.0")}),-1.0]])]});
            var Q47;
            Q47=makeQuery(id+"F0.imprint","IMPRINT",FACE,{"disambiguationData":[TD([[makeQuery(id+"F0.imprint","IMPRINT",EDGE,{"derivedFrom":sQuery(id+"F0.wireOp",EDGE,"E26.4.4.0")}),-1.0]])]});
            var Q48;
            Q48=makeQuery(id+"F0.imprint","IMPRINT",FACE,{"disambiguationData":[TD([[makeQuery(id+"F0.imprint","IMPRINT",EDGE,{"derivedFrom":sQuery(id+"F0.wireOp",EDGE,"E26.5.2.0")}),-1.0]])]});
            var Q49;
            Q49=makeQuery(id+"F0.imprint","IMPRINT",FACE,{"disambiguationData":[TD([[makeQuery(id+"F0.imprint","IMPRINT",EDGE,{"derivedFrom":sQuery(id+"F0.wireOp",EDGE,"E26.5.1.0")}),-1.0]])]});
            extrude(context, id + "F1", {"entities" : qUnion([Q0, Q1, Q2, Q3, Q4, Q5, Q6, Q7, Q8, Q9, Q10, Q11, Q12, Q13, Q14, Q15, Q16, Q17, Q18, Q19, Q20, Q21, Q22, Q23, Q24, Q25, Q26, Q27, Q28, Q29, Q30, Q31, Q32, Q33, Q34, Q35, Q36, Q37, Q38, Q39, Q40, Q41, Q42, Q43, Q44, Q45, Q46, Q47, Q48, Q49]), "depth" : 2 * mm, "offsetDistance" : 25.4 * mm});
        }
        {
            var Q0;
            Q0=qCreatedBy(makeId("Top.planeOp"),FACE);
            var sketch = newSketch(context, id + "F2", { "sketchPlane" : qUnion([Q0])});
            skLineSegment(sketch, "E39.bottom", {"start": v(28.58, 15.88) * mm, "end": v(-28.57, 15.88) * mm});
            skLineSegment(sketch, "E39.top", {"start": v(28.57, -15.88) * mm, "end": v(-28.58, -15.88) * mm});
            skLineSegment(sketch, "E39.left", {"start": v(28.58, 15.88) * mm, "end": v(28.57, -15.87) * mm});
            skLineSegment(sketch, "E39.right", {"start": v(-28.57, 15.88) * mm, "end": v(-28.58, -15.88) * mm});
            skPoint(sketch, "E39.middle", {"position": v(0, 0) * mm});
            skLineSegment(sketch, "E40.0", {"start": v(28.83, 16.13) * mm, "end": v(-28.83, 16.13) * mm});
            skLineSegment(sketch, "E40.1", {"start": v(28.83, 16.13) * mm, "end": v(28.83, -16.13) * mm});
            skLineSegment(sketch, "E40.2", {"start": v(28.83, -16.13) * mm, "end": v(-28.83, -16.13) * mm});
            skLineSegment(sketch, "E40.3", {"start": v(-28.83, 16.13) * mm, "end": v(-28.83, -16.13) * mm});
            skSolve(sketch);
        }
        {
            var Q0;
            Q0=qSketchRegion(id+"F2",true);
            extrude(context, id + "F3", {"entities" : qUnion([Q0]), "depth" : 2 * mm, "offsetDistance" : 25.4 * mm});
        }
        {
            var Q0;
            Q0=qCreatedBy(makeId("Top.planeOp"),FACE);
            var sketch = newSketch(context, id + "F4", { "sketchPlane" : qUnion([Q0])});
            skLineSegment(sketch, "E41.bottom", {"start": v(28.58, 15.88) * mm, "end": v(-28.57, 15.88) * mm});
            skLineSegment(sketch, "E41.top", {"start": v(28.57, -15.88) * mm, "end": v(-28.58, -15.88) * mm});
            skLineSegment(sketch, "E41.left", {"start": v(28.58, 15.88) * mm, "end": v(28.57, -15.88) * mm});
            skLineSegment(sketch, "E41.right", {"start": v(-28.57, 15.88) * mm, "end": v(-28.58, -15.88) * mm});
            skPoint(sketch, "E41.middle", {"position": v(0, 0) * mm});
            skSolve(sketch);
        }
        {
            var Q0;
            Q0=qSketchRegion(id+"F4",true);
            extrude(context, id + "F5", {"entities" : qUnion([Q0]), "depth" : .5 * mm, "offsetDistance" : 25.4 * mm});
        }
    });
